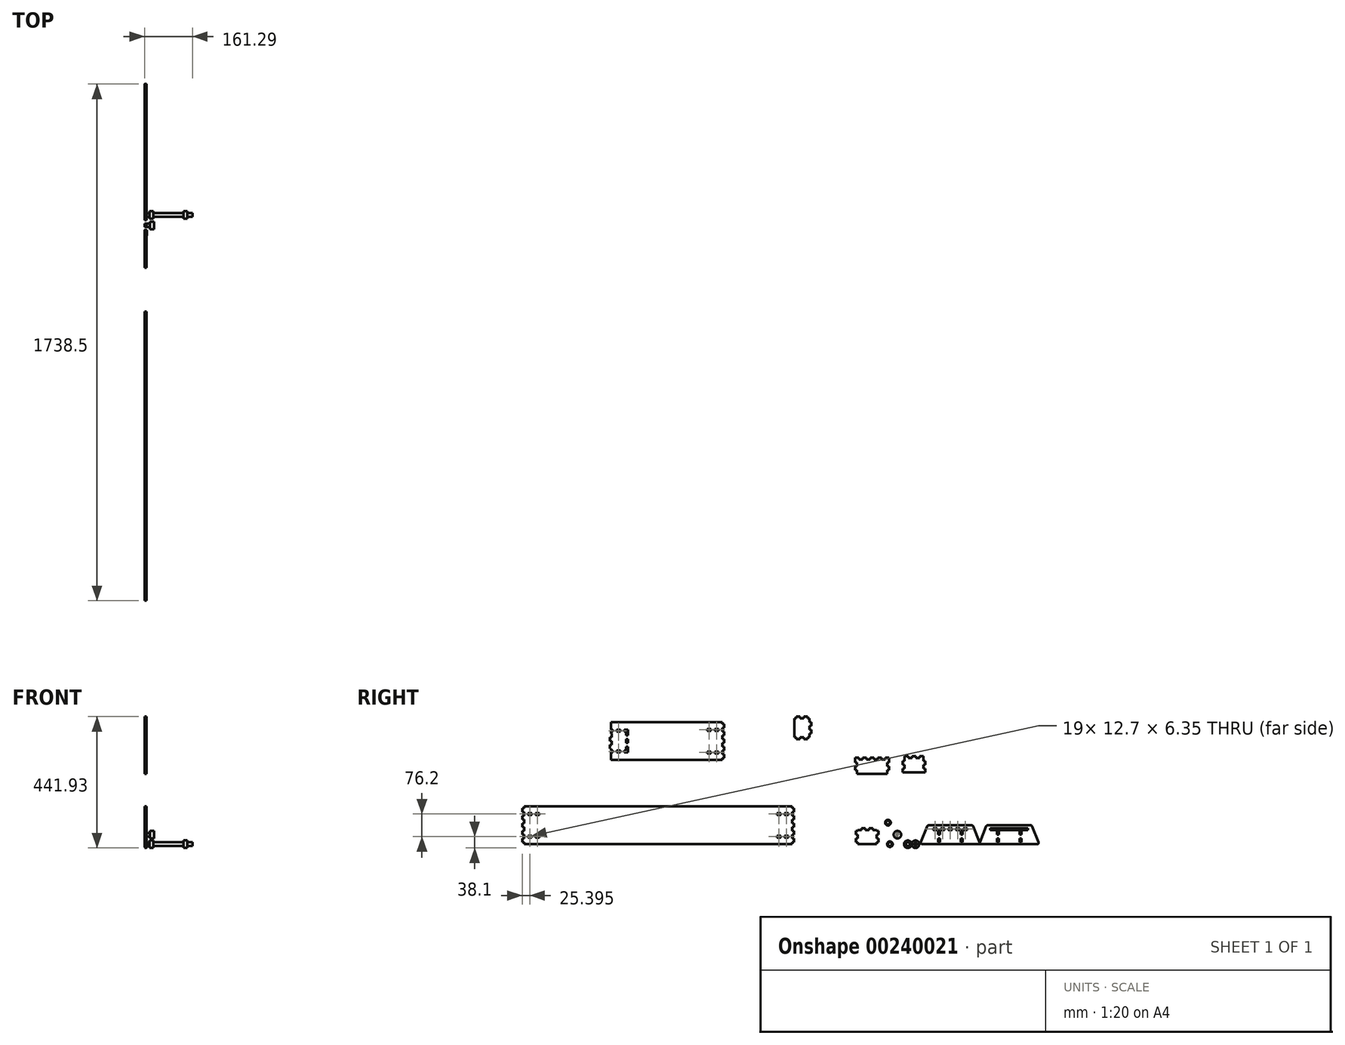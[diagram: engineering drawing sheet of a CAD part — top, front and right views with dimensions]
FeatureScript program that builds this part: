
annotation { "Feature Type Name" : "Feature", "Feature Type Description" : "" }
export const myFeature = defineFeature(function(context is Context, id is Id, definition is map)
    precondition{}
    {
        {
            var Q0;
            Q0=qCreatedBy(makeId("Right.planeOp"),FACE);
            var sketch = newSketch(context, id + "F0", { "sketchPlane" : qUnion([Q0])});
            skLineSegment(sketch, "E0.bottom", {"start": v(0, 0) * mm, "end": v(152.4, 0) * mm});
            skLineSegment(sketch, "E0.top", {"start": v(0, 101.6) * mm, "end": v(152.4, 101.6) * mm});
            skLineSegment(sketch, "E0.left", {"start": v(0, 0) * mm, "end": v(0, 101.6) * mm});
            skLineSegment(sketch, "E0.right", {"start": v(152.4, 0) * mm, "end": v(152.4, 101.6) * mm});
            skLineSegment(sketch, "E1", {"start": v(76.2, 101.6) * mm, "end": v(76.2, 0) * mm, "construction": true});
            skLineSegment(sketch, "E2", {"start": v(0, 50.8) * mm, "end": v(152.4, 50.8) * mm, "construction": true});
            skLineSegment(sketch, "E3", {"start": v(76.2, 53.98) * mm, "end": v(82.55, 53.98) * mm});
            skLineSegment(sketch, "E4", {"start": v(82.55, 53.98) * mm, "end": v(82.55, 50.8) * mm});
            skLineSegment(sketch, "E5.MirrorCS", {"start": v(69.85, 53.98) * mm, "end": v(69.85, 50.8) * mm});
            skLineSegment(sketch, "E6.MirrorCS", {"start": v(76.2, 53.98) * mm, "end": v(69.85, 53.98) * mm});
            skLineSegment(sketch, "E7.MirrorCS", {"start": v(82.55, 47.63) * mm, "end": v(82.55, 50.8) * mm});
            skLineSegment(sketch, "E8.MirrorCS", {"start": v(76.2, 47.63) * mm, "end": v(82.55, 47.63) * mm});
            skLineSegment(sketch, "E9.MirrorCS", {"start": v(76.2, 47.63) * mm, "end": v(69.85, 47.63) * mm});
            skLineSegment(sketch, "E10.MirrorCS", {"start": v(69.85, 47.63) * mm, "end": v(69.85, 50.8) * mm});
            skLineSegment(sketch, "E11.1.0.0", {"start": v(101.6, 53.98) * mm, "end": v(107.95, 53.98) * mm});
            skLineSegment(sketch, "E11.1.0.1", {"start": v(101.6, 53.98) * mm, "end": v(95.25, 53.98) * mm});
            skLineSegment(sketch, "E11.1.0.2", {"start": v(95.25, 53.98) * mm, "end": v(95.25, 50.8) * mm});
            skLineSegment(sketch, "E11.1.0.3", {"start": v(95.25, 47.63) * mm, "end": v(95.25, 50.8) * mm});
            skLineSegment(sketch, "E11.1.0.4", {"start": v(101.6, 47.63) * mm, "end": v(95.25, 47.63) * mm});
            skLineSegment(sketch, "E11.1.0.5", {"start": v(101.6, 47.63) * mm, "end": v(107.95, 47.63) * mm});
            skLineSegment(sketch, "E11.1.0.6", {"start": v(107.95, 47.63) * mm, "end": v(107.95, 50.8) * mm});
            skLineSegment(sketch, "E11.1.0.7", {"start": v(107.95, 53.98) * mm, "end": v(107.95, 50.8) * mm});
            skLineSegment(sketch, "E11.2.0.0", {"start": v(127, 53.98) * mm, "end": v(133.35, 53.98) * mm});
            skLineSegment(sketch, "E11.2.0.1", {"start": v(127, 53.98) * mm, "end": v(120.65, 53.98) * mm});
            skLineSegment(sketch, "E11.2.0.2", {"start": v(120.65, 53.98) * mm, "end": v(120.65, 50.8) * mm});
            skLineSegment(sketch, "E11.2.0.3", {"start": v(120.65, 47.63) * mm, "end": v(120.65, 50.8) * mm});
            skLineSegment(sketch, "E11.2.0.4", {"start": v(127, 47.63) * mm, "end": v(120.65, 47.63) * mm});
            skLineSegment(sketch, "E11.2.0.5", {"start": v(127, 47.63) * mm, "end": v(133.35, 47.63) * mm});
            skLineSegment(sketch, "E11.2.0.6", {"start": v(133.35, 47.63) * mm, "end": v(133.35, 50.8) * mm});
            skLineSegment(sketch, "E11.2.0.7", {"start": v(133.35, 53.98) * mm, "end": v(133.35, 50.8) * mm});
            skLineSegment(sketch, "E11.direction1", {"start": v(76.2, 53.98) * mm, "end": v(101.6, 53.98) * mm, "construction": true});
            skLineSegment(sketch, "E11.direction2", {"start": v(76.2, 53.98) * mm, "end": v(25.4, 53.98) * mm, "construction": true});
            skLineSegment(sketch, "E12.0.0.1", {"start": v(25.4, 53.97) * mm, "end": v(31.75, 53.98) * mm});
            skLineSegment(sketch, "E12.3.0.1", {"start": v(25.4, 53.97) * mm, "end": v(19.05, 53.97) * mm});
            skLineSegment(sketch, "E12.6.0.1", {"start": v(19.05, 53.98) * mm, "end": v(19.05, 50.8) * mm});
            skLineSegment(sketch, "E12.9.0.1", {"start": v(19.05, 47.62) * mm, "end": v(19.05, 50.8) * mm});
            skLineSegment(sketch, "E12.12.0.1", {"start": v(25.4, 47.63) * mm, "end": v(19.05, 47.63) * mm});
            skLineSegment(sketch, "E12.15.0.1", {"start": v(25.4, 47.63) * mm, "end": v(31.75, 47.63) * mm});
            skLineSegment(sketch, "E12.18.0.1", {"start": v(31.75, 47.62) * mm, "end": v(31.75, 50.8) * mm});
            skLineSegment(sketch, "E12.21.0.1", {"start": v(31.75, 53.98) * mm, "end": v(31.75, 50.8) * mm});
            skLineSegment(sketch, "E12.0.1.1", {"start": v(50.8, 53.97) * mm, "end": v(57.15, 53.98) * mm});
            skLineSegment(sketch, "E12.3.1.1", {"start": v(50.8, 53.97) * mm, "end": v(44.45, 53.97) * mm});
            skLineSegment(sketch, "E12.6.1.1", {"start": v(44.45, 53.98) * mm, "end": v(44.45, 50.8) * mm});
            skLineSegment(sketch, "E12.9.1.1", {"start": v(44.45, 47.62) * mm, "end": v(44.45, 50.8) * mm});
            skLineSegment(sketch, "E12.12.1.1", {"start": v(50.8, 47.63) * mm, "end": v(44.45, 47.63) * mm});
            skLineSegment(sketch, "E12.15.1.1", {"start": v(50.8, 47.63) * mm, "end": v(57.15, 47.63) * mm});
            skLineSegment(sketch, "E12.18.1.1", {"start": v(57.15, 47.62) * mm, "end": v(57.15, 50.8) * mm});
            skLineSegment(sketch, "E12.21.1.1", {"start": v(57.15, 53.98) * mm, "end": v(57.15, 50.8) * mm});
            skLineSegment(sketch, "E13.bottom", {"start": v(34.93, 44.45) * mm, "end": v(41.28, 44.45) * mm});
            skLineSegment(sketch, "E13.top", {"start": v(34.93, 31.75) * mm, "end": v(41.28, 31.75) * mm});
            skLineSegment(sketch, "E13.left", {"start": v(34.93, 44.45) * mm, "end": v(34.93, 31.75) * mm});
            skLineSegment(sketch, "E13.right", {"start": v(41.28, 44.45) * mm, "end": v(41.28, 31.75) * mm});
            skLineSegment(sketch, "E14.0.1.0", {"start": v(41.28, 19.05) * mm, "end": v(41.28, 6.35) * mm});
            skLineSegment(sketch, "E14.0.1.1", {"start": v(34.93, 19.05) * mm, "end": v(41.28, 19.05) * mm});
            skLineSegment(sketch, "E14.0.1.2", {"start": v(34.93, 19.05) * mm, "end": v(34.93, 6.35) * mm});
            skLineSegment(sketch, "E14.0.1.3", {"start": v(34.93, 6.35) * mm, "end": v(41.28, 6.35) * mm});
            skLineSegment(sketch, "E14.direction1", {"start": v(41.28, 31.75) * mm, "end": v(53.98, 31.75) * mm, "construction": true});
            skLineSegment(sketch, "E14.direction2", {"start": v(41.28, 31.75) * mm, "end": v(41.28, 6.35) * mm, "construction": true});
            skLineSegment(sketch, "E15.MirrorCS", {"start": v(111.12, 44.45) * mm, "end": v(111.12, 31.75) * mm});
            skLineSegment(sketch, "E16.MirrorCS", {"start": v(117.47, 44.45) * mm, "end": v(111.12, 44.45) * mm});
            skLineSegment(sketch, "E17.MirrorCS", {"start": v(117.47, 44.45) * mm, "end": v(117.47, 31.75) * mm});
            skLineSegment(sketch, "E18.MirrorCS", {"start": v(117.47, 31.75) * mm, "end": v(111.12, 31.75) * mm});
            skLineSegment(sketch, "E19.MirrorCS", {"start": v(117.47, 19.05) * mm, "end": v(111.12, 19.05) * mm});
            skLineSegment(sketch, "E20.MirrorCS", {"start": v(117.47, 19.05) * mm, "end": v(117.47, 6.35) * mm});
            skLineSegment(sketch, "E21.MirrorCS", {"start": v(117.47, 6.35) * mm, "end": v(111.12, 6.35) * mm});
            skLineSegment(sketch, "E22.MirrorCS", {"start": v(111.12, 31.75) * mm, "end": v(111.12, 6.35) * mm, "construction": true});
            skLineSegment(sketch, "E23", {"start": v(111.12, 19.05) * mm, "end": v(111.12, 6.35) * mm});
            skSolve(sketch);
        }
        {
            var Q0;
            Q0=makeQuery(id+"F0.imprint","IMPRINT",FACE,{"disambiguationData":[TD([[makeQuery(id+"F0.imprint","IMPRINT",EDGE,{"derivedFrom":sQuery(id+"F0.wireOp",EDGE,"E0.bottom")}),1.0]])]});
            extrude(context, id + "F1", {"entities" : qUnion([Q0]), "depth" : 6.35 * mm});
        }
        {
            var Q0;
            Q0=qCreatedBy(makeId("Right.planeOp"),FACE);
            var sketch = newSketch(context, id + "F2", { "sketchPlane" : qUnion([Q0])});
            skLineSegment(sketch, "E24.bottom", {"start": v(198.38, 0) * mm, "end": v(350.78, 0) * mm});
            skLineSegment(sketch, "E24.top", {"start": v(198.38, 101.6) * mm, "end": v(350.78, 101.6) * mm});
            skLineSegment(sketch, "E24.left", {"start": v(198.38, 0) * mm, "end": v(198.38, 101.6) * mm});
            skLineSegment(sketch, "E24.right", {"start": v(350.78, 0) * mm, "end": v(350.78, 101.6) * mm});
            skLineSegment(sketch, "E25", {"start": v(198.38, 50.8) * mm, "end": v(350.78, 50.8) * mm, "construction": true});
            skLineSegment(sketch, "E26.bottom", {"start": v(211.08, 53.98) * mm, "end": v(338.08, 53.98) * mm});
            skLineSegment(sketch, "E26.top", {"start": v(211.08, 47.63) * mm, "end": v(338.08, 47.63) * mm});
            skLineSegment(sketch, "E26.left", {"start": v(211.08, 53.98) * mm, "end": v(211.08, 47.63) * mm});
            skLineSegment(sketch, "E26.right", {"start": v(338.08, 53.98) * mm, "end": v(338.08, 47.63) * mm});
            skLineSegment(sketch, "E27.bottom", {"start": v(233.3, 44.45) * mm, "end": v(239.66, 44.45) * mm});
            skLineSegment(sketch, "E27.top", {"start": v(233.3, 31.75) * mm, "end": v(239.66, 31.75) * mm});
            skLineSegment(sketch, "E27.left", {"start": v(233.3, 44.45) * mm, "end": v(233.3, 31.75) * mm});
            skLineSegment(sketch, "E27.right", {"start": v(239.66, 44.45) * mm, "end": v(239.66, 31.75) * mm});
            skLineSegment(sketch, "E28.bottom", {"start": v(233.3, 19.05) * mm, "end": v(239.66, 19.05) * mm});
            skLineSegment(sketch, "E28.top", {"start": v(233.3, 6.35) * mm, "end": v(239.66, 6.35) * mm});
            skLineSegment(sketch, "E28.left", {"start": v(233.3, 19.05) * mm, "end": v(233.3, 6.35) * mm});
            skLineSegment(sketch, "E28.right", {"start": v(239.66, 19.05) * mm, "end": v(239.66, 6.35) * mm});
            skLineSegment(sketch, "E29", {"start": v(274.58, 101.6) * mm, "end": v(274.58, 0) * mm, "construction": true});
            skLineSegment(sketch, "E30.MirrorCS", {"start": v(315.86, 44.45) * mm, "end": v(309.5, 44.45) * mm});
            skLineSegment(sketch, "E31.MirrorCS", {"start": v(315.86, 31.75) * mm, "end": v(309.5, 31.75) * mm});
            skLineSegment(sketch, "E32.MirrorCS", {"start": v(315.86, 44.45) * mm, "end": v(315.86, 31.75) * mm});
            skLineSegment(sketch, "E33.MirrorCS", {"start": v(315.86, 19.05) * mm, "end": v(315.86, 6.35) * mm});
            skLineSegment(sketch, "E34.MirrorCS", {"start": v(315.86, 6.35) * mm, "end": v(309.5, 6.35) * mm});
            skLineSegment(sketch, "E35.MirrorCS", {"start": v(309.5, 19.05) * mm, "end": v(309.5, 6.35) * mm});
            skLineSegment(sketch, "E36.MirrorCS", {"start": v(309.5, 44.45) * mm, "end": v(309.5, 31.75) * mm});
            skLineSegment(sketch, "E37.MirrorCS", {"start": v(315.86, 19.05) * mm, "end": v(309.5, 19.05) * mm});
            skSolve(sketch);
        }
        {
            var Q0;
            Q0=makeQuery(id+"F2.imprint","IMPRINT",FACE,{"disambiguationData":[TD([[makeQuery(id+"F2.imprint","IMPRINT",EDGE,{"derivedFrom":sQuery(id+"F2.wireOp",EDGE,"E24.bottom")}),1.0]])]});
            extrude(context, id + "F3", {"entities" : qUnion([Q0]), "depth" : 6.35 * mm});
        }
        {
            var Q0;
            Q0=qCreatedBy(makeId("Right.planeOp"),FACE);
            var sketch = newSketch(context, id + "F4", { "sketchPlane" : qUnion([Q0])});
            skLineSegment(sketch, "E38.bottom", {"start": v(-164.83, 0) * mm, "end": v(-241.03, 0) * mm});
            skLineSegment(sketch, "E38.top", {"start": v(-164.83, 53.98) * mm, "end": v(-241.03, 53.98) * mm});
            skLineSegment(sketch, "E38.left", {"start": v(-164.83, 0) * mm, "end": v(-164.83, 53.97) * mm});
            skLineSegment(sketch, "E38.right", {"start": v(-241.03, 0) * mm, "end": v(-241.03, 53.98) * mm});
            skLineSegment(sketch, "E39.bottom", {"start": v(-164.83, 0) * mm, "end": v(-171.18, 0) * mm});
            skLineSegment(sketch, "E39.top", {"start": v(-164.83, 6.35) * mm, "end": v(-171.18, 6.35) * mm});
            skLineSegment(sketch, "E39.left", {"start": v(-164.83, 0) * mm, "end": v(-164.83, 6.35) * mm});
            skLineSegment(sketch, "E39.right", {"start": v(-171.18, 0) * mm, "end": v(-171.18, 6.35) * mm});
            skLineSegment(sketch, "E40.bottom", {"start": v(-164.83, 19.05) * mm, "end": v(-171.18, 19.05) * mm});
            skLineSegment(sketch, "E40.top", {"start": v(-164.83, 31.75) * mm, "end": v(-171.18, 31.75) * mm});
            skLineSegment(sketch, "E40.left", {"start": v(-164.83, 19.05) * mm, "end": v(-164.83, 31.75) * mm});
            skLineSegment(sketch, "E40.right", {"start": v(-171.18, 19.05) * mm, "end": v(-171.18, 31.75) * mm});
            skLineSegment(sketch, "E41.bottom", {"start": v(-164.83, 53.98) * mm, "end": v(-171.18, 53.98) * mm});
            skLineSegment(sketch, "E41.top", {"start": v(-164.83, 47.62) * mm, "end": v(-171.18, 47.62) * mm});
            skLineSegment(sketch, "E41.left", {"start": v(-164.83, 53.98) * mm, "end": v(-164.83, 47.62) * mm});
            skLineSegment(sketch, "E42", {"start": v(-202.93, 53.98) * mm, "end": v(-202.93, 0) * mm, "construction": true});
            skLineSegment(sketch, "E43.MirrorCS", {"start": v(-241.03, 47.62) * mm, "end": v(-234.68, 47.62) * mm});
            skLineSegment(sketch, "E44.MirrorCS", {"start": v(-234.68, 53.98) * mm, "end": v(-234.68, 47.62) * mm});
            skLineSegment(sketch, "E45.MirrorCS", {"start": v(-234.68, 19.05) * mm, "end": v(-234.68, 31.75) * mm});
            skLineSegment(sketch, "E46.MirrorCS", {"start": v(-241.03, 31.75) * mm, "end": v(-234.68, 31.75) * mm});
            skLineSegment(sketch, "E47.MirrorCS", {"start": v(-241.03, 19.05) * mm, "end": v(-234.68, 19.05) * mm});
            skLineSegment(sketch, "E48.MirrorCS", {"start": v(-234.68, 0) * mm, "end": v(-234.68, 6.35) * mm});
            skLineSegment(sketch, "E49.MirrorCS", {"start": v(-241.03, 6.35) * mm, "end": v(-234.68, 6.35) * mm});
            skLineSegment(sketch, "E50.bottom", {"start": v(-183.88, 53.98) * mm, "end": v(-196.58, 53.98) * mm});
            skLineSegment(sketch, "E51.bottom", {"start": v(-171.18, 53.98) * mm, "end": v(-183.88, 53.98) * mm});
            skLineSegment(sketch, "E51.top", {"start": v(-171.18, 47.62) * mm, "end": v(-183.88, 47.62) * mm});
            skLineSegment(sketch, "E51.left", {"start": v(-171.18, 53.98) * mm, "end": v(-171.18, 47.62) * mm});
            skLineSegment(sketch, "E51.right", {"start": v(-183.88, 53.98) * mm, "end": v(-183.88, 47.62) * mm});
            skLineSegment(sketch, "E52.MirrorCS", {"start": v(-234.68, 47.62) * mm, "end": v(-221.98, 47.62) * mm});
            skLineSegment(sketch, "E53.MirrorCS", {"start": v(-221.98, 53.98) * mm, "end": v(-221.98, 47.62) * mm});
            skLineSegment(sketch, "E54.bottom", {"start": v(-196.58, 53.98) * mm, "end": v(-202.93, 53.98) * mm});
            skLineSegment(sketch, "E54.top", {"start": v(-196.58, 47.62) * mm, "end": v(-202.93, 47.62) * mm});
            skLineSegment(sketch, "E54.left", {"start": v(-196.58, 53.98) * mm, "end": v(-196.58, 47.62) * mm});
            skLineSegment(sketch, "E54.right", {"start": v(-202.93, 53.98) * mm, "end": v(-202.93, 47.62) * mm});
            skLineSegment(sketch, "E55.MirrorCS", {"start": v(-209.28, 47.62) * mm, "end": v(-202.93, 47.62) * mm});
            skLineSegment(sketch, "E56.MirrorCS", {"start": v(-209.28, 53.98) * mm, "end": v(-209.28, 47.62) * mm});
            skLineSegment(sketch, "E57.top", {"start": v(-164.83, 44.45) * mm, "end": v(-171.18, 44.45) * mm});
            skLineSegment(sketch, "E57.left", {"start": v(-164.83, 47.62) * mm, "end": v(-164.83, 44.45) * mm});
            skLineSegment(sketch, "E57.right", {"start": v(-171.18, 47.62) * mm, "end": v(-171.18, 44.45) * mm});
            skLineSegment(sketch, "E58.MirrorCS", {"start": v(-234.68, 47.62) * mm, "end": v(-234.68, 44.45) * mm});
            skLineSegment(sketch, "E59.MirrorCS", {"start": v(-241.03, 44.45) * mm, "end": v(-234.68, 44.45) * mm});
            skSolve(sketch);
        }
        {
            var Q0;
            {var subQ4=sQuery(id+"F4.wireOp",EDGE,"E39.top");Q0=makeQuery(id+"F4.imprint","IMPRINT",FACE,{"disambiguationData":[TD([[makeQuery(id+"F4.imprint","IMPRINT",EDGE,{"derivedFrom":subQ4}),-1.0]])]});}
            extrude(context, id + "F5", {"entities" : qUnion([Q0]), "depth" : 6.35 * mm});
        }
        {
            var Q0;
            Q0=qCreatedBy(makeId("Right.planeOp"),FACE);
            var sketch = newSketch(context, id + "F6", { "sketchPlane" : qUnion([Q0])});
            skLineSegment(sketch, "E60.bottom", {"start": v(-450.34, 0) * mm, "end": v(-1364.74, 0) * mm});
            skLineSegment(sketch, "E60.top", {"start": v(-450.34, 127) * mm, "end": v(-1364.74, 127) * mm});
            skLineSegment(sketch, "E60.left", {"start": v(-450.34, 0) * mm, "end": v(-450.34, 127) * mm});
            skLineSegment(sketch, "E60.right", {"start": v(-1364.74, 0) * mm, "end": v(-1364.74, 127) * mm});
            skLineSegment(sketch, "E61.bottom", {"start": v(-450.34, 127) * mm, "end": v(-456.7, 127) * mm});
            skLineSegment(sketch, "E61.top", {"start": v(-450.34, 120.65) * mm, "end": v(-456.7, 120.65) * mm});
            skLineSegment(sketch, "E61.left", {"start": v(-450.34, 127) * mm, "end": v(-450.34, 120.65) * mm});
            skLineSegment(sketch, "E61.right", {"start": v(-456.7, 127) * mm, "end": v(-456.7, 120.65) * mm});
            skLineSegment(sketch, "E62.bottom", {"start": v(-450.34, 107.95) * mm, "end": v(-456.7, 107.95) * mm});
            skLineSegment(sketch, "E62.top", {"start": v(-450.34, 95.25) * mm, "end": v(-456.7, 95.25) * mm});
            skLineSegment(sketch, "E62.left", {"start": v(-450.34, 107.95) * mm, "end": v(-450.34, 95.25) * mm});
            skLineSegment(sketch, "E62.right", {"start": v(-456.7, 107.95) * mm, "end": v(-456.7, 95.25) * mm});
            skLineSegment(sketch, "E63.0.1.0", {"start": v(-456.7, 82.55) * mm, "end": v(-456.7, 69.85) * mm});
            skLineSegment(sketch, "E63.0.1.1", {"start": v(-450.34, 69.85) * mm, "end": v(-456.7, 69.85) * mm});
            skLineSegment(sketch, "E63.0.1.2", {"start": v(-450.34, 82.55) * mm, "end": v(-456.7, 82.55) * mm});
            skLineSegment(sketch, "E63.0.2.0", {"start": v(-456.7, 57.15) * mm, "end": v(-456.7, 44.45) * mm});
            skLineSegment(sketch, "E63.0.2.1", {"start": v(-450.34, 44.45) * mm, "end": v(-456.7, 44.45) * mm});
            skLineSegment(sketch, "E63.0.2.2", {"start": v(-450.34, 57.15) * mm, "end": v(-456.7, 57.15) * mm});
            skLineSegment(sketch, "E63.0.3.0", {"start": v(-456.7, 31.75) * mm, "end": v(-456.7, 19.05) * mm});
            skLineSegment(sketch, "E63.0.3.1", {"start": v(-450.34, 19.05) * mm, "end": v(-456.7, 19.05) * mm});
            skLineSegment(sketch, "E63.0.3.2", {"start": v(-450.34, 31.75) * mm, "end": v(-456.7, 31.75) * mm});
            skLineSegment(sketch, "E63.direction1", {"start": v(-456.7, 95.25) * mm, "end": v(-431.3, 95.25) * mm, "construction": true});
            skLineSegment(sketch, "E63.direction2", {"start": v(-456.7, 95.25) * mm, "end": v(-456.7, 69.85) * mm, "construction": true});
            skLineSegment(sketch, "E64", {"start": v(-450.34, 63.5) * mm, "end": v(-1364.74, 63.5) * mm, "construction": true});
            skLineSegment(sketch, "E65.MirrorCS", {"start": v(-450.34, 6.35) * mm, "end": v(-456.7, 6.35) * mm});
            skLineSegment(sketch, "E66.MirrorCS", {"start": v(-456.7, 0) * mm, "end": v(-456.7, 6.35) * mm});
            skLineSegment(sketch, "E67.left", {"start": v(-456.7, 104.78) * mm, "end": v(-456.7, 98.43) * mm});
            skLineSegment(sketch, "E68.direction1", {"start": v(-456.7, 69.85) * mm, "end": v(-482.1, 69.85) * mm, "construction": true});
            skLineSegment(sketch, "E69.MirrorCS", {"start": v(-456.7, 31.75) * mm, "end": v(-456.7, 57.15) * mm, "construction": true});
            skLineSegment(sketch, "E70", {"start": v(-907.54, 0) * mm, "end": v(-907.54, 127) * mm, "construction": true});
            skLineSegment(sketch, "E71.MirrorCS", {"start": v(-1364.74, 127) * mm, "end": v(-1358.4, 127) * mm});
            skLineSegment(sketch, "E72.MirrorCS", {"start": v(-1358.4, 104.77) * mm, "end": v(-1358.4, 98.42) * mm});
            skLineSegment(sketch, "E73.MirrorCS", {"start": v(-1358.4, 82.55) * mm, "end": v(-1358.4, 69.85) * mm});
            skLineSegment(sketch, "E74.MirrorCS", {"start": v(-1364.74, 95.25) * mm, "end": v(-1358.4, 95.25) * mm});
            skLineSegment(sketch, "E75.MirrorCS", {"start": v(-1364.74, 107.95) * mm, "end": v(-1358.4, 107.95) * mm});
            skLineSegment(sketch, "E76.MirrorCS", {"start": v(-1364.74, 120.65) * mm, "end": v(-1358.4, 120.65) * mm});
            skLineSegment(sketch, "E77.MirrorCS", {"start": v(-1358.4, 127) * mm, "end": v(-1358.4, 120.65) * mm});
            skLineSegment(sketch, "E78.MirrorCS", {"start": v(-1364.74, 127) * mm, "end": v(-1364.74, 120.65) * mm});
            skLineSegment(sketch, "E79.MirrorCS", {"start": v(-1364.74, 19.05) * mm, "end": v(-1358.4, 19.05) * mm});
            skLineSegment(sketch, "E80.MirrorCS", {"start": v(-1364.74, 44.45) * mm, "end": v(-1358.4, 44.45) * mm});
            skLineSegment(sketch, "E81.MirrorCS", {"start": v(-1358.4, 107.95) * mm, "end": v(-1358.4, 95.25) * mm});
            skLineSegment(sketch, "E82.MirrorCS", {"start": v(-1364.74, 31.75) * mm, "end": v(-1358.4, 31.75) * mm});
            skLineSegment(sketch, "E83.MirrorCS", {"start": v(-1364.74, 57.15) * mm, "end": v(-1358.4, 57.15) * mm});
            skLineSegment(sketch, "E84.MirrorCS", {"start": v(-1364.74, 6.35) * mm, "end": v(-1358.4, 6.35) * mm});
            skLineSegment(sketch, "E85.MirrorCS", {"start": v(-1364.74, 82.55) * mm, "end": v(-1358.4, 82.55) * mm});
            skLineSegment(sketch, "E86.MirrorCS", {"start": v(-1364.74, 69.85) * mm, "end": v(-1358.4, 69.85) * mm});
            skLineSegment(sketch, "E87.MirrorCS", {"start": v(-1358.4, 95.25) * mm, "end": v(-1358.4, 69.85) * mm, "construction": true});
            skLineSegment(sketch, "E88.MirrorCS", {"start": v(-1358.4, 0) * mm, "end": v(-1358.4, 6.35) * mm});
            skLineSegment(sketch, "E89.MirrorCS", {"start": v(-1358.4, 57.15) * mm, "end": v(-1358.4, 44.45) * mm});
            skLineSegment(sketch, "E90.MirrorCS", {"start": v(-1358.4, 69.85) * mm, "end": v(-1333, 69.85) * mm, "construction": true});
            skLineSegment(sketch, "E91.MirrorCS", {"start": v(-1364.74, 107.95) * mm, "end": v(-1364.74, 95.25) * mm});
            skLineSegment(sketch, "E92.MirrorCS", {"start": v(-1358.4, 31.75) * mm, "end": v(-1358.4, 19.05) * mm});
            skLineSegment(sketch, "E93.MirrorCS", {"start": v(-1364.74, 63.5) * mm, "end": v(-450.34, 63.5) * mm, "construction": true});
            skLineSegment(sketch, "E94.MirrorCS", {"start": v(-1358.4, 31.75) * mm, "end": v(-1358.4, 57.15) * mm, "construction": true});
            skLineSegment(sketch, "E95.MirrorCS", {"start": v(-1358.4, 95.25) * mm, "end": v(-1383.8, 95.25) * mm, "construction": true});
            skLineSegment(sketch, "E96.MirrorCS", {"start": v(-1364.74, 127) * mm, "end": v(-450.34, 127) * mm});
            skLineSegment(sketch, "E97.MirrorCS", {"start": v(-1364.74, 0) * mm, "end": v(-450.34, 0) * mm});
            skLineSegment(sketch, "E98", {"start": v(-456.7, 28.58) * mm, "end": v(-456.7, 22.23) * mm});
            skLineSegment(sketch, "E99", {"start": v(-1358.4, 28.57) * mm, "end": v(-1358.4, 22.22) * mm});
            skLineSegment(sketch, "E100.bottom", {"start": v(-469.4, 104.78) * mm, "end": v(-482.1, 104.78) * mm});
            skLineSegment(sketch, "E100.top", {"start": v(-469.4, 98.43) * mm, "end": v(-482.1, 98.43) * mm});
            skLineSegment(sketch, "E100.left", {"start": v(-469.4, 104.78) * mm, "end": v(-469.4, 98.43) * mm});
            skLineSegment(sketch, "E100.right", {"start": v(-482.1, 104.78) * mm, "end": v(-482.1, 98.43) * mm});
            skLineSegment(sketch, "E101.1.0.0", {"start": v(-494.8, 104.78) * mm, "end": v(-494.8, 98.43) * mm});
            skLineSegment(sketch, "E101.1.0.1", {"start": v(-507.5, 104.78) * mm, "end": v(-507.5, 98.43) * mm});
            skLineSegment(sketch, "E101.1.0.2", {"start": v(-494.8, 98.43) * mm, "end": v(-507.5, 98.43) * mm});
            skLineSegment(sketch, "E101.1.0.3", {"start": v(-494.8, 104.78) * mm, "end": v(-507.5, 104.78) * mm});
            skLineSegment(sketch, "E101.direction1", {"start": v(-482.1, 98.43) * mm, "end": v(-507.5, 98.43) * mm, "construction": true});
            skLineSegment(sketch, "E102.MirrorCS", {"start": v(-494.8, 28.57) * mm, "end": v(-507.5, 28.57) * mm});
            skLineSegment(sketch, "E103.MirrorCS", {"start": v(-507.5, 22.23) * mm, "end": v(-507.5, 28.58) * mm});
            skLineSegment(sketch, "E104.MirrorCS", {"start": v(-482.1, 28.57) * mm, "end": v(-507.5, 28.57) * mm, "construction": true});
            skLineSegment(sketch, "E105.MirrorCS", {"start": v(-482.1, 22.23) * mm, "end": v(-482.1, 28.58) * mm});
            skLineSegment(sketch, "E106.MirrorCS", {"start": v(-469.4, 22.23) * mm, "end": v(-469.4, 28.58) * mm});
            skLineSegment(sketch, "E107.MirrorCS", {"start": v(-469.4, 28.57) * mm, "end": v(-482.1, 28.57) * mm});
            skLineSegment(sketch, "E108.MirrorCS", {"start": v(-469.4, 22.22) * mm, "end": v(-482.1, 22.22) * mm});
            skLineSegment(sketch, "E109.MirrorCS", {"start": v(-494.8, 22.23) * mm, "end": v(-494.8, 28.58) * mm});
            skLineSegment(sketch, "E110.MirrorCS", {"start": v(-494.8, 22.22) * mm, "end": v(-507.5, 22.22) * mm});
            skLineSegment(sketch, "E111.MirrorCS", {"start": v(-1307.6, 104.77) * mm, "end": v(-1307.6, 98.42) * mm});
            skLineSegment(sketch, "E112.MirrorCS", {"start": v(-1320.3, 22.22) * mm, "end": v(-1320.3, 28.57) * mm});
            skLineSegment(sketch, "E113.MirrorCS", {"start": v(-1333, 22.22) * mm, "end": v(-1333, 28.57) * mm});
            skLineSegment(sketch, "E114.MirrorCS", {"start": v(-1307.6, 22.22) * mm, "end": v(-1307.6, 28.57) * mm});
            skLineSegment(sketch, "E115.MirrorCS", {"start": v(-1345.7, 104.77) * mm, "end": v(-1345.7, 98.42) * mm});
            skLineSegment(sketch, "E116.MirrorCS", {"start": v(-1333, 104.77) * mm, "end": v(-1333, 98.42) * mm});
            skLineSegment(sketch, "E117.MirrorCS", {"start": v(-1345.7, 22.22) * mm, "end": v(-1345.7, 28.57) * mm});
            skLineSegment(sketch, "E118.MirrorCS", {"start": v(-1320.3, 104.77) * mm, "end": v(-1320.3, 98.42) * mm});
            skLineSegment(sketch, "E119.MirrorCS", {"start": v(-1320.3, 28.57) * mm, "end": v(-1307.6, 28.57) * mm});
            skLineSegment(sketch, "E120.MirrorCS", {"start": v(-1345.7, 98.43) * mm, "end": v(-1333, 98.43) * mm});
            skLineSegment(sketch, "E121.MirrorCS", {"start": v(-1345.7, 104.78) * mm, "end": v(-1333, 104.78) * mm});
            skLineSegment(sketch, "E122.MirrorCS", {"start": v(-1320.3, 104.78) * mm, "end": v(-1307.6, 104.78) * mm});
            skLineSegment(sketch, "E123.MirrorCS", {"start": v(-1320.3, 98.43) * mm, "end": v(-1307.6, 98.43) * mm});
            skLineSegment(sketch, "E124.MirrorCS", {"start": v(-1333, 28.57) * mm, "end": v(-1307.6, 28.57) * mm, "construction": true});
            skLineSegment(sketch, "E125.MirrorCS", {"start": v(-1345.7, 28.57) * mm, "end": v(-1333, 28.57) * mm});
            skLineSegment(sketch, "E126.MirrorCS", {"start": v(-1320.3, 22.22) * mm, "end": v(-1307.6, 22.22) * mm});
            skLineSegment(sketch, "E127.MirrorCS", {"start": v(-1345.7, 22.22) * mm, "end": v(-1333, 22.22) * mm});
            skLineSegment(sketch, "E128.MirrorCS", {"start": v(-1333, 98.43) * mm, "end": v(-1307.6, 98.43) * mm, "construction": true});
            skSolve(sketch);
        }
        {
            var Q0;
            {var subQ4=sQuery(id+"F6.wireOp",EDGE,"E61.top");Q0=makeQuery(id+"F6.imprint","IMPRINT",FACE,{"disambiguationData":[TD([[makeQuery(id+"F6.imprint","IMPRINT",EDGE,{"derivedFrom":subQ4}),1.0]])]});}
            extrude(context, id + "F7", {"entities" : qUnion([Q0]), "depth" : 6.35 * mm});
        }
        {
            var Q0;
            Q0=qCreatedBy(makeId("Right.planeOp"),FACE);
            var sketch = newSketch(context, id + "F8", { "sketchPlane" : qUnion([Q0])});
            skCircle(sketch, "E129", {"center": v(-101.6, 32.09) * mm, "radius": 5.72 * mm});
            skSolve(sketch);
        }
        {
            var Q0;
            Q0=makeQuery(id+"F8.imprint","IMPRINT",FACE,{"disambiguationData":[TD([[makeQuery(id+"F8.imprint","IMPRINT",EDGE,{"derivedFrom":sQuery(id+"F8.wireOp",EDGE,"E129")}),1.0]])]});
            extrude(context, id + "F9", {"entities" : qUnion([Q0]), "depth" : 19.05 * mm});
        }
        {
            var Q0;
            Q0=qCreatedBy(makeId("Right.planeOp"),FACE);
            var sketch = newSketch(context, id + "F10", { "sketchPlane" : qUnion([Q0])});
            skCircle(sketch, "E130", {"center": v(-66.73, 0) * mm, "radius": 5.72 * mm});
            skSolve(sketch);
        }
        {
            var Q0;
            Q0=makeQuery(id+"F10.imprint","IMPRINT",FACE,{"disambiguationData":[TD([[makeQuery(id+"F10.imprint","IMPRINT",EDGE,{"derivedFrom":sQuery(id+"F10.wireOp",EDGE,"E130")}),1.0]])]});
            extrude(context, id + "F11", {"entities" : qUnion([Q0]), "depth" : 17.14 * mm});
        }
        {
            var Q0;
            Q0=makeQuery(id+"F11.opExtrude","CAP_FACE",FACE,{"disambiguationData":[OSD([sQuery(id+"F10.wireOp",EDGE,"E130")])],"isStart":false});
            var sketch = newSketch(context, id + "F12", { "sketchPlane" : qUnion([Q0])});
            skCircle(sketch, "E131", {"center": v(-66.73, 0) * mm, "radius": 12.7 * mm});
            skSolve(sketch);
        }
        {
            var Q0;
            Q0=makeQuery(id+"F12.imprint","IMPRINT",FACE,{"disambiguationData":[TD([[makeQuery(id+"F12.imprint","IMPRINT",EDGE,{"derivedFrom":sQuery(id+"F12.wireOp",EDGE,"E131")}),1.0]])]});
            var Q1;
            Q1=makeQuery(id+"F12.imprint","IMPRINT",FACE,{"disambiguationData":[TD([[makeQuery(id+"F12.imprint","IMPRINT",EDGE,{"derivedFrom":makeQuery(id+"F11.opExtrude","CAP_EDGE",EDGE,{"disambiguationData":[OSD([sQuery(id+"F10.wireOp",EDGE,"E130")])],"isStart":false})}),1.0]])]});
            extrude(context, id + "F13", {"entities" : qUnion([Q0, Q1]), "operationType" : NewBodyOperationType.ADD, "depth" : 12.7 * mm});
        }
        {
            var Q0;
            Q0=makeQuery(id+"F13.opExtrude","CAP_FACE",FACE,{"disambiguationData":[OSD([sQuery(id+"F12.wireOp",EDGE,"E131")])],"isStart":false});
            var sketch = newSketch(context, id + "F14", { "sketchPlane" : qUnion([Q0])});
            skCircle(sketch, "E132", {"center": v(-66.73, 0) * mm, "radius": 6.35 * mm});
            skSolve(sketch);
        }
        {
            var Q0;
            Q0=makeQuery(id+"F14.imprint","IMPRINT",FACE,{"disambiguationData":[TD([[makeQuery(id+"F14.imprint","IMPRINT",EDGE,{"derivedFrom":sQuery(id+"F14.wireOp",EDGE,"E132")}),1.0]])]});
            extrude(context, id + "F15", {"entities" : qUnion([Q0]), "operationType" : NewBodyOperationType.ADD, "depth" : 101.6 * mm});
        }
        {
            var Q0;
            Q0=makeQuery(id+"F15.opExtrude","CAP_FACE",FACE,{"disambiguationData":[OSD([sQuery(id+"F14.wireOp",EDGE,"E132")])],"isStart":false});
            var sketch = newSketch(context, id + "F16", { "sketchPlane" : qUnion([Q0])});
            skCircle(sketch, "E133", {"center": v(-66.73, 0) * mm, "radius": 12.7 * mm});
            skSolve(sketch);
        }
        {
            var Q0;
            Q0=makeQuery(id+"F16.imprint","IMPRINT",FACE,{"disambiguationData":[TD([[makeQuery(id+"F16.imprint","IMPRINT",EDGE,{"derivedFrom":sQuery(id+"F16.wireOp",EDGE,"E133")}),1.0]])]});
            var Q1;
            Q1=makeQuery(id+"F16.imprint","IMPRINT",FACE,{"disambiguationData":[TD([[makeQuery(id+"F16.imprint","IMPRINT",EDGE,{"derivedFrom":makeQuery(id+"F15.opExtrude","CAP_EDGE",EDGE,{"disambiguationData":[OSD([sQuery(id+"F14.wireOp",EDGE,"E132")])],"isStart":false})}),1.0]])]});
            extrude(context, id + "F17", {"entities" : qUnion([Q0, Q1]), "operationType" : NewBodyOperationType.ADD, "depth" : 12.7 * mm});
        }
        {
            var Q0;
            Q0=makeQuery(id+"F17.opExtrude","CAP_FACE",FACE,{"disambiguationData":[OSD([sQuery(id+"F16.wireOp",EDGE,"E133")])],"isStart":false});
            var sketch = newSketch(context, id + "F18", { "sketchPlane" : qUnion([Q0])});
            skCircle(sketch, "E134", {"center": v(-66.73, 0) * mm, "radius": 6.35 * mm});
            skSolve(sketch);
        }
        {
            var Q0;
            Q0=makeQuery(id+"F18.imprint","IMPRINT",FACE,{"disambiguationData":[TD([[makeQuery(id+"F18.imprint","IMPRINT",EDGE,{"derivedFrom":sQuery(id+"F18.wireOp",EDGE,"E134")}),1.0]])]});
            extrude(context, id + "F19", {"entities" : qUnion([Q0]), "operationType" : NewBodyOperationType.ADD, "depth" : 17.14 * mm});
        }
        {
            var Q0;
            Q0=makeQuery(id+"F9.opExtrude","CAP_FACE",FACE,{"disambiguationData":[OSD([sQuery(id+"F8.wireOp",EDGE,"E129")])],"isStart":false});
            var sketch = newSketch(context, id + "F20", { "sketchPlane" : qUnion([Q0])});
            skCircle(sketch, "E135", {"center": v(-101.6, 32.09) * mm, "radius": 12.7 * mm});
            skSolve(sketch);
        }
        {
            var Q0;
            Q0=makeQuery(id+"F20.imprint","IMPRINT",FACE,{"disambiguationData":[TD([[makeQuery(id+"F20.imprint","IMPRINT",EDGE,{"derivedFrom":sQuery(id+"F20.wireOp",EDGE,"E135")}),1.0]])]});
            var Q1;
            Q1=makeQuery(id+"F20.imprint","IMPRINT",FACE,{"disambiguationData":[TD([[makeQuery(id+"F20.imprint","IMPRINT",EDGE,{"derivedFrom":makeQuery(id+"F9.opExtrude","CAP_EDGE",EDGE,{"disambiguationData":[OSD([sQuery(id+"F8.wireOp",EDGE,"E129")])],"isStart":false})}),1.0]])]});
            extrude(context, id + "F21", {"entities" : qUnion([Q0, Q1]), "operationType" : NewBodyOperationType.ADD, "depth" : 12.7 * mm});
        }
        {
            var Q0;
            Q0=qCreatedBy(makeId("Top.planeOp"),FACE);
            var sketch = newSketch(context, id + "F22", { "sketchPlane" : qUnion([Q0])});
            skCircle(sketch, "E136", {"center": v(4.76, -101.6) * mm, "radius": 1.59 * mm});
            skSolve(sketch);
        }
        {
            var Q0;
            Q0 = qSketchRegion(id + "F22", true);
            extrude(context, id + "F23", {"entities" : qUnion([Q0]), "operationType" : NewBodyOperationType.REMOVE, "endBound" : BoundingType.THROUGH_ALL, "depth" : 25.4 * mm});
        }
        {
            var Q0;
            Q0=qCreatedBy(makeId("Right.planeOp"),FACE);
            var sketch = newSketch(context, id + "F24", { "sketchPlane" : qUnion([Q0])});
            skCircle(sketch, "E137", {"center": v(-127, 0) * mm, "radius": 9.53 * mm});
            skSolve(sketch);
        }
        {
            var Q0;
            Q0=makeQuery(id+"F24.imprint","IMPRINT",FACE,{"disambiguationData":[TD([[makeQuery(id+"F24.imprint","IMPRINT",EDGE,{"derivedFrom":sQuery(id+"F24.wireOp",EDGE,"E137")}),1.0]])]});
            extrude(context, id + "F25", {"entities" : qUnion([Q0]), "depth" : 8.47 * mm});
        }
        {
            var Q0;
            Q0=qCreatedBy(makeId("Top.planeOp"),FACE);
            var sketch = newSketch(context, id + "F26", { "sketchPlane" : qUnion([Q0])});
            skCircle(sketch, "E138", {"center": v(4.23, -127) * mm, "radius": 1.59 * mm});
            skSolve(sketch);
        }
        {
            var Q0;
            Q0 = qSketchRegion(id + "F26", true);
            extrude(context, id + "F27", {"entities" : qUnion([Q0]), "operationType" : NewBodyOperationType.REMOVE, "endBound" : BoundingType.THROUGH_ALL, "depth" : 25.4 * mm});
        }
        {
            var Q0;
            Q0=makeQuery(id+"F25.opExtrude","CAP_FACE",FACE,{"disambiguationData":[OSD([sQuery(id+"F24.wireOp",EDGE,"E137")])],"isStart":true});
            var sketch = newSketch(context, id + "F28", { "sketchPlane" : qUnion([Q0])});
            skCircle(sketch, "E139", {"center": v(127, 0) * mm, "radius": 6.35 * mm});
            skSolve(sketch);
        }
        {
            var Q0;
            Q0=makeQuery(id+"F28.imprint","IMPRINT",FACE,{"disambiguationData":[TD([[makeQuery(id+"F28.imprint","IMPRINT",EDGE,{"derivedFrom":sQuery(id+"F28.wireOp",EDGE,"E139")}),1.0]])]});
            extrude(context, id + "F29", {"entities" : qUnion([Q0]), "operationType" : NewBodyOperationType.REMOVE, "endBound" : BoundingType.UP_TO_NEXT, "oppositeDirection" : true, "depth" : 25.4 * mm});
        }
        {
            var Q0;
            Q0=qCreatedBy(makeId("Right.planeOp"),FACE);
            var sketch = newSketch(context, id + "F30", { "sketchPlane" : qUnion([Q0])});
            skCircle(sketch, "E140", {"center": v(-133.45, 72.65) * mm, "radius": 9.53 * mm});
            skCircle(sketch, "E141", {"center": v(-133.45, 72.65) * mm, "radius": 6.35 * mm});
            skSolve(sketch);
        }
        {
            var Q0;
            Q0=makeQuery(id+"F30.imprint","IMPRINT",FACE,{"disambiguationData":[TD([[makeQuery(id+"F30.imprint","IMPRINT",EDGE,{"derivedFrom":sQuery(id+"F30.wireOp",EDGE,"E140")}),1.0]])]});
            extrude(context, id + "F31", {"entities" : qUnion([Q0]), "depth" : 2.38 * mm});
        }
        {
            var Q0;
            Q0=makeQuery(id+"F5.opExtrude","SWEPT_BODY",BODY,{"disambiguationData":[OSD([sQuery(id+"F4.wireOp",EDGE,"E38.bottom"),sQuery(id+"F4.wireOp",EDGE,"E38.top"),sQuery(id+"F4.wireOp",EDGE,"E38.left"),sQuery(id+"F4.wireOp",EDGE,"E38.right"),sQuery(id+"F4.wireOp",EDGE,"E39.top"),sQuery(id+"F4.wireOp",EDGE,"E39.right"),sQuery(id+"F4.wireOp",EDGE,"E40.bottom"),sQuery(id+"F4.wireOp",EDGE,"E40.top"),sQuery(id+"F4.wireOp",EDGE,"E40.right"),sQuery(id+"F4.wireOp",EDGE,"E45.MirrorCS"),sQuery(id+"F4.wireOp",EDGE,"E46.MirrorCS"),sQuery(id+"F4.wireOp",EDGE,"E47.MirrorCS"),sQuery(id+"F4.wireOp",EDGE,"E48.MirrorCS"),sQuery(id+"F4.wireOp",EDGE,"E49.MirrorCS"),sQuery(id+"F4.wireOp",EDGE,"E50.bottom"),sQuery(id+"F4.wireOp",EDGE,"E51.top"),sQuery(id+"F4.wireOp",EDGE,"E51.right"),sQuery(id+"F4.wireOp",EDGE,"E52.MirrorCS"),sQuery(id+"F4.wireOp",EDGE,"E53.MirrorCS"),sQuery(id+"F4.wireOp",EDGE,"E54.top"),sQuery(id+"F4.wireOp",EDGE,"E54.left"),sQuery(id+"F4.wireOp",EDGE,"E55.MirrorCS"),sQuery(id+"F4.wireOp",EDGE,"E56.MirrorCS"),sQuery(id+"F4.wireOp",EDGE,"E57.top"),sQuery(id+"F4.wireOp",EDGE,"E57.right"),sQuery(id+"F4.wireOp",EDGE,"E58.MirrorCS"),sQuery(id+"F4.wireOp",EDGE,"E59.MirrorCS")])]});
            transform(context, id + "F32", {"entities" : qUnion([Q0]), "transformType" : TransformType.TRANSLATION_3D, "dx" : 0 * mm, "dy" : 0 * mm, "dz" : 0 * mm, "makeCopy" : true});
        }
        {
            var Q0;
            Q0=makeQuery(id+"F32.opPattern","COPY",BODY,{"derivedFrom":makeQuery(id+"F5.opExtrude","SWEPT_BODY",BODY,{"disambiguationData":[OSD([sQuery(id+"F4.wireOp",EDGE,"E38.bottom"),sQuery(id+"F4.wireOp",EDGE,"E38.top"),sQuery(id+"F4.wireOp",EDGE,"E38.left"),sQuery(id+"F4.wireOp",EDGE,"E38.right"),sQuery(id+"F4.wireOp",EDGE,"E39.top"),sQuery(id+"F4.wireOp",EDGE,"E39.right"),sQuery(id+"F4.wireOp",EDGE,"E40.bottom"),sQuery(id+"F4.wireOp",EDGE,"E40.top"),sQuery(id+"F4.wireOp",EDGE,"E40.right"),sQuery(id+"F4.wireOp",EDGE,"E45.MirrorCS"),sQuery(id+"F4.wireOp",EDGE,"E46.MirrorCS"),sQuery(id+"F4.wireOp",EDGE,"E47.MirrorCS"),sQuery(id+"F4.wireOp",EDGE,"E48.MirrorCS"),sQuery(id+"F4.wireOp",EDGE,"E49.MirrorCS"),sQuery(id+"F4.wireOp",EDGE,"E50.bottom"),sQuery(id+"F4.wireOp",EDGE,"E51.top"),sQuery(id+"F4.wireOp",EDGE,"E51.right"),sQuery(id+"F4.wireOp",EDGE,"E52.MirrorCS"),sQuery(id+"F4.wireOp",EDGE,"E53.MirrorCS"),sQuery(id+"F4.wireOp",EDGE,"E54.top"),sQuery(id+"F4.wireOp",EDGE,"E54.left"),sQuery(id+"F4.wireOp",EDGE,"E55.MirrorCS"),sQuery(id+"F4.wireOp",EDGE,"E56.MirrorCS"),sQuery(id+"F4.wireOp",EDGE,"E57.top"),sQuery(id+"F4.wireOp",EDGE,"E57.right"),sQuery(id+"F4.wireOp",EDGE,"E58.MirrorCS"),sQuery(id+"F4.wireOp",EDGE,"E59.MirrorCS")])]}),"instanceName":"1"});
            deleteBodies(context, id + "F33", {"entities" : qUnion([Q0])});
        }
        {
            var Q0;
            Q0=qCreatedBy(makeId("Right.planeOp"),FACE);
            var sketch = newSketch(context, id + "F34", { "sketchPlane" : qUnion([Q0])});
            skLineSegment(sketch, "E142.bottom", {"start": v(-244.06, 237.28) * mm, "end": v(-129.76, 237.28) * mm});
            skLineSegment(sketch, "E142.top", {"start": v(-244.06, 291.25) * mm, "end": v(-129.76, 291.25) * mm});
            skLineSegment(sketch, "E142.left", {"start": v(-244.06, 237.28) * mm, "end": v(-244.06, 291.25) * mm});
            skLineSegment(sketch, "E142.right", {"start": v(-129.76, 237.28) * mm, "end": v(-129.76, 291.25) * mm});
            skLineSegment(sketch, "E143.bottom", {"start": v(-244.06, 237.28) * mm, "end": v(-237.71, 237.28) * mm});
            skLineSegment(sketch, "E143.top", {"start": v(-244.06, 249.98) * mm, "end": v(-237.71, 249.98) * mm});
            skLineSegment(sketch, "E143.left", {"start": v(-244.06, 237.28) * mm, "end": v(-244.06, 249.98) * mm});
            skLineSegment(sketch, "E143.right", {"start": v(-237.71, 237.28) * mm, "end": v(-237.71, 249.98) * mm});
            skLineSegment(sketch, "E144.bottom", {"start": v(-244.06, 275.38) * mm, "end": v(-237.71, 275.38) * mm});
            skLineSegment(sketch, "E144.top", {"start": v(-244.06, 262.68) * mm, "end": v(-237.71, 262.68) * mm});
            skLineSegment(sketch, "E144.left", {"start": v(-244.06, 275.38) * mm, "end": v(-244.06, 262.68) * mm});
            skLineSegment(sketch, "E144.right", {"start": v(-237.71, 275.38) * mm, "end": v(-237.71, 262.68) * mm});
            skLineSegment(sketch, "E145.bottom", {"start": v(-231.36, 291.25) * mm, "end": v(-218.66, 291.25) * mm});
            skLineSegment(sketch, "E145.top", {"start": v(-231.36, 284.9) * mm, "end": v(-218.66, 284.9) * mm});
            skLineSegment(sketch, "E145.left", {"start": v(-231.36, 291.25) * mm, "end": v(-231.36, 284.9) * mm});
            skLineSegment(sketch, "E145.right", {"start": v(-218.66, 291.25) * mm, "end": v(-218.66, 284.9) * mm});
            skLineSegment(sketch, "E146.1.0.0", {"start": v(-205.96, 291.25) * mm, "end": v(-205.96, 284.9) * mm});
            skLineSegment(sketch, "E146.1.0.1", {"start": v(-193.26, 291.25) * mm, "end": v(-193.26, 284.9) * mm});
            skLineSegment(sketch, "E146.1.0.2", {"start": v(-205.96, 291.25) * mm, "end": v(-193.26, 291.25) * mm});
            skLineSegment(sketch, "E146.1.0.3", {"start": v(-205.96, 284.9) * mm, "end": v(-193.26, 284.9) * mm});
            skLineSegment(sketch, "E146.2.0.0", {"start": v(-180.56, 291.25) * mm, "end": v(-180.56, 284.9) * mm});
            skLineSegment(sketch, "E146.2.0.1", {"start": v(-167.86, 291.25) * mm, "end": v(-167.86, 284.9) * mm});
            skLineSegment(sketch, "E146.2.0.2", {"start": v(-180.56, 291.25) * mm, "end": v(-167.86, 291.25) * mm});
            skLineSegment(sketch, "E146.2.0.3", {"start": v(-180.56, 284.9) * mm, "end": v(-167.86, 284.9) * mm});
            skLineSegment(sketch, "E146.3.0.0", {"start": v(-155.16, 291.25) * mm, "end": v(-155.16, 284.9) * mm});
            skLineSegment(sketch, "E146.3.0.1", {"start": v(-142.46, 291.25) * mm, "end": v(-142.46, 284.9) * mm});
            skLineSegment(sketch, "E146.3.0.2", {"start": v(-155.16, 291.25) * mm, "end": v(-142.46, 291.25) * mm});
            skLineSegment(sketch, "E146.3.0.3", {"start": v(-155.16, 284.9) * mm, "end": v(-142.46, 284.9) * mm});
            skLineSegment(sketch, "E146.direction1", {"start": v(-244.06, 291.25) * mm, "end": v(-218.66, 291.25) * mm, "construction": true});
            skLineSegment(sketch, "E147", {"start": v(-186.91, 291.25) * mm, "end": v(-186.91, 237.28) * mm, "construction": true});
            skLineSegment(sketch, "E148.MirrorCS", {"start": v(-129.76, 262.68) * mm, "end": v(-136.11, 262.68) * mm});
            skLineSegment(sketch, "E149.MirrorCS", {"start": v(-129.76, 275.38) * mm, "end": v(-136.11, 275.38) * mm});
            skLineSegment(sketch, "E150.MirrorCS", {"start": v(-136.11, 275.38) * mm, "end": v(-136.11, 262.68) * mm});
            skLineSegment(sketch, "E151.MirrorCS", {"start": v(-129.76, 249.98) * mm, "end": v(-136.11, 249.98) * mm});
            skLineSegment(sketch, "E152.MirrorCS", {"start": v(-136.11, 237.28) * mm, "end": v(-136.11, 249.98) * mm});
            skSolve(sketch);
        }
        {
            var Q0;
            {var subQ6=sQuery(id+"F34.wireOp",EDGE,"E143.top");Q0=makeQuery(id+"F34.imprint","IMPRINT",FACE,{"disambiguationData":[TD([[makeQuery(id+"F34.imprint","IMPRINT",EDGE,{"derivedFrom":subQ6}),1.0]])]});}
            extrude(context, id + "F35", {"entities" : qUnion([Q0]), "depth" : 6.35 * mm});
        }
        {
            var Q0;
            Q0=qCreatedBy(makeId("Right.planeOp"),FACE);
            var sketch = newSketch(context, id + "F36", { "sketchPlane" : qUnion([Q0])});
            skLineSegment(sketch, "E153.bottom", {"start": v(-83.94, 241.82) * mm, "end": v(-7.74, 241.82) * mm});
            skLineSegment(sketch, "E153.top", {"start": v(-83.94, 295.8) * mm, "end": v(-7.74, 295.8) * mm});
            skLineSegment(sketch, "E153.left", {"start": v(-83.94, 241.82) * mm, "end": v(-83.94, 295.8) * mm});
            skLineSegment(sketch, "E153.right", {"start": v(-7.74, 241.82) * mm, "end": v(-7.74, 295.8) * mm});
            skLineSegment(sketch, "E154.bottom", {"start": v(-83.94, 295.8) * mm, "end": v(-77.59, 295.8) * mm});
            skLineSegment(sketch, "E154.top", {"start": v(-83.94, 279.92) * mm, "end": v(-77.59, 279.92) * mm});
            skLineSegment(sketch, "E154.left", {"start": v(-83.94, 295.8) * mm, "end": v(-83.94, 279.92) * mm});
            skLineSegment(sketch, "E154.right", {"start": v(-77.59, 295.8) * mm, "end": v(-77.59, 279.92) * mm});
            skLineSegment(sketch, "E155.bottom", {"start": v(-83.94, 254.52) * mm, "end": v(-77.59, 254.52) * mm});
            skLineSegment(sketch, "E155.top", {"start": v(-83.94, 267.22) * mm, "end": v(-77.59, 267.22) * mm});
            skLineSegment(sketch, "E155.left", {"start": v(-83.94, 254.52) * mm, "end": v(-83.94, 267.22) * mm});
            skLineSegment(sketch, "E155.right", {"start": v(-77.59, 254.52) * mm, "end": v(-77.59, 267.22) * mm});
            skLineSegment(sketch, "E156.bottom", {"start": v(-64.89, 295.8) * mm, "end": v(-52.19, 295.8) * mm});
            skLineSegment(sketch, "E156.top", {"start": v(-64.89, 289.44) * mm, "end": v(-52.19, 289.44) * mm});
            skLineSegment(sketch, "E156.left", {"start": v(-64.89, 295.8) * mm, "end": v(-64.89, 289.44) * mm});
            skLineSegment(sketch, "E156.right", {"start": v(-52.19, 295.8) * mm, "end": v(-52.19, 289.44) * mm});
            skLineSegment(sketch, "E157.1.0.0", {"start": v(-26.79, 295.8) * mm, "end": v(-26.79, 289.44) * mm});
            skLineSegment(sketch, "E157.1.0.1", {"start": v(-39.49, 289.44) * mm, "end": v(-26.79, 289.44) * mm});
            skLineSegment(sketch, "E157.1.0.2", {"start": v(-39.49, 295.8) * mm, "end": v(-39.49, 289.44) * mm});
            skLineSegment(sketch, "E157.direction1", {"start": v(-64.89, 289.44) * mm, "end": v(-39.49, 289.44) * mm, "construction": true});
            skLineSegment(sketch, "E158", {"start": v(-45.84, 241.82) * mm, "end": v(-45.84, 295.8) * mm, "construction": true});
            skLineSegment(sketch, "E159.MirrorCS", {"start": v(-7.74, 254.52) * mm, "end": v(-14.09, 254.52) * mm});
            skLineSegment(sketch, "E160.MirrorCS", {"start": v(-7.74, 267.22) * mm, "end": v(-14.09, 267.22) * mm});
            skLineSegment(sketch, "E161.MirrorCS", {"start": v(-7.74, 279.92) * mm, "end": v(-14.09, 279.92) * mm});
            skLineSegment(sketch, "E162.MirrorCS", {"start": v(-14.09, 295.8) * mm, "end": v(-14.09, 279.92) * mm});
            skLineSegment(sketch, "E163.MirrorCS", {"start": v(-14.09, 254.52) * mm, "end": v(-14.09, 267.22) * mm});
            skSolve(sketch);
        }
        {
            var Q0;
            {var subQ13=sQuery(id+"F36.wireOp",EDGE,"E153.bottom");Q0=makeQuery(id+"F36.imprint","IMPRINT",FACE,{"disambiguationData":[TD([[makeQuery(id+"F36.imprint","IMPRINT",EDGE,{"derivedFrom":subQ13}),1.0]])]});}
            extrude(context, id + "F37", {"entities" : qUnion([Q0]), "depth" : 6.35 * mm});
        }
        {
            var Q0;
            Q0=qCreatedBy(makeId("Right.planeOp"),FACE);
            var sketch = newSketch(context, id + "F38", { "sketchPlane" : qUnion([Q0])});
            skLineSegment(sketch, "E164.bottom", {"start": v(-505.29, 353.03) * mm, "end": v(-390.99, 353.03) * mm});
            skLineSegment(sketch, "E164.top", {"start": v(-505.29, 429.23) * mm, "end": v(-390.99, 429.23) * mm});
            skLineSegment(sketch, "E164.left", {"start": v(-505.29, 353.03) * mm, "end": v(-505.29, 429.23) * mm});
            skLineSegment(sketch, "E164.right", {"start": v(-390.99, 353.03) * mm, "end": v(-390.99, 429.23) * mm});
            skLineSegment(sketch, "E165.bottom", {"start": v(-505.29, 429.23) * mm, "end": v(-492.59, 429.23) * mm});
            skLineSegment(sketch, "E165.top", {"start": v(-505.29, 422.88) * mm, "end": v(-492.59, 422.88) * mm});
            skLineSegment(sketch, "E165.left", {"start": v(-505.29, 429.23) * mm, "end": v(-505.29, 422.88) * mm});
            skLineSegment(sketch, "E165.right", {"start": v(-492.59, 429.23) * mm, "end": v(-492.59, 422.88) * mm});
            skLineSegment(sketch, "E166", {"start": v(-448.14, 429.23) * mm, "end": v(-448.14, 353.03) * mm, "construction": true});
            skLineSegment(sketch, "E167.1.0.0", {"start": v(-467.19, 429.23) * mm, "end": v(-467.19, 422.88) * mm});
            skLineSegment(sketch, "E167.1.0.1", {"start": v(-479.89, 422.88) * mm, "end": v(-467.19, 422.88) * mm});
            skLineSegment(sketch, "E167.1.0.2", {"start": v(-479.89, 429.23) * mm, "end": v(-467.19, 429.23) * mm});
            skLineSegment(sketch, "E167.1.0.3", {"start": v(-479.89, 429.23) * mm, "end": v(-479.89, 422.88) * mm});
            skLineSegment(sketch, "E167.2.0.0", {"start": v(-441.79, 429.23) * mm, "end": v(-441.79, 422.88) * mm});
            skLineSegment(sketch, "E167.2.0.1", {"start": v(-454.49, 422.88) * mm, "end": v(-441.79, 422.88) * mm});
            skLineSegment(sketch, "E167.2.0.2", {"start": v(-454.49, 429.23) * mm, "end": v(-441.79, 429.23) * mm});
            skLineSegment(sketch, "E167.2.0.3", {"start": v(-454.49, 429.23) * mm, "end": v(-454.49, 422.88) * mm});
            skLineSegment(sketch, "E167.3.0.0", {"start": v(-416.39, 429.23) * mm, "end": v(-416.39, 422.88) * mm});
            skLineSegment(sketch, "E167.3.0.1", {"start": v(-429.09, 422.88) * mm, "end": v(-416.39, 422.88) * mm});
            skLineSegment(sketch, "E167.3.0.2", {"start": v(-429.09, 429.23) * mm, "end": v(-416.39, 429.23) * mm});
            skLineSegment(sketch, "E167.3.0.3", {"start": v(-429.09, 429.23) * mm, "end": v(-429.09, 422.88) * mm});
            skLineSegment(sketch, "E167.4.0.0", {"start": v(-390.99, 429.23) * mm, "end": v(-390.99, 422.88) * mm});
            skLineSegment(sketch, "E167.4.0.1", {"start": v(-403.69, 422.88) * mm, "end": v(-390.99, 422.88) * mm});
            skLineSegment(sketch, "E167.4.0.2", {"start": v(-403.69, 429.23) * mm, "end": v(-390.99, 429.23) * mm});
            skLineSegment(sketch, "E167.4.0.3", {"start": v(-403.69, 429.23) * mm, "end": v(-403.69, 422.88) * mm});
            skLineSegment(sketch, "E167.direction1", {"start": v(-505.29, 422.88) * mm, "end": v(-479.89, 422.88) * mm, "construction": true});
            skPoint(sketch, "E168.oppositeSnap0", {"position": v(-498.94, 422.88) * mm});
            skLineSegment(sketch, "E168.bottom", {"start": v(-505.29, 359.38) * mm, "end": v(-498.94, 359.38) * mm});
            skLineSegment(sketch, "E168.top", {"start": v(-505.29, 372.08) * mm, "end": v(-498.94, 372.08) * mm});
            skLineSegment(sketch, "E168.left", {"start": v(-505.29, 359.38) * mm, "end": v(-505.29, 372.08) * mm});
            skLineSegment(sketch, "E168.right", {"start": v(-498.94, 359.38) * mm, "end": v(-498.94, 372.08) * mm});
            skLineSegment(sketch, "E169.0.1.0", {"start": v(-498.94, 384.78) * mm, "end": v(-498.94, 397.48) * mm});
            skLineSegment(sketch, "E169.0.1.1", {"start": v(-505.29, 384.78) * mm, "end": v(-498.94, 384.78) * mm});
            skLineSegment(sketch, "E169.0.1.2", {"start": v(-505.29, 397.48) * mm, "end": v(-498.94, 397.48) * mm});
            skLineSegment(sketch, "E169.0.1.3", {"start": v(-505.29, 384.78) * mm, "end": v(-505.29, 397.48) * mm});
            skLineSegment(sketch, "E169.0.2.0", {"start": v(-498.94, 410.18) * mm, "end": v(-498.94, 422.88) * mm});
            skLineSegment(sketch, "E169.0.2.1", {"start": v(-505.29, 410.18) * mm, "end": v(-498.94, 410.18) * mm});
            skLineSegment(sketch, "E169.0.2.2", {"start": v(-505.29, 422.88) * mm, "end": v(-498.94, 422.88) * mm});
            skLineSegment(sketch, "E169.0.2.3", {"start": v(-505.29, 410.18) * mm, "end": v(-505.29, 422.88) * mm});
            skLineSegment(sketch, "E169.direction1", {"start": v(-505.29, 359.38) * mm, "end": v(-479.89, 359.38) * mm, "construction": true});
            skLineSegment(sketch, "E169.direction2", {"start": v(-505.29, 359.38) * mm, "end": v(-505.29, 384.78) * mm, "construction": true});
            skLineSegment(sketch, "E170", {"start": v(-505.29, 391.13) * mm, "end": v(-390.99, 391.13) * mm, "construction": true});
            skLineSegment(sketch, "E171.MirrorCS", {"start": v(-505.29, 359.38) * mm, "end": v(-492.59, 359.38) * mm});
            skLineSegment(sketch, "E172.MirrorCS", {"start": v(-479.89, 359.38) * mm, "end": v(-467.19, 359.38) * mm});
            skLineSegment(sketch, "E173.MirrorCS", {"start": v(-467.19, 353.03) * mm, "end": v(-467.19, 359.38) * mm});
            skLineSegment(sketch, "E174.MirrorCS", {"start": v(-479.89, 353.03) * mm, "end": v(-479.89, 359.38) * mm});
            skLineSegment(sketch, "E175.MirrorCS", {"start": v(-429.09, 359.38) * mm, "end": v(-416.39, 359.38) * mm});
            skLineSegment(sketch, "E176.MirrorCS", {"start": v(-492.59, 353.03) * mm, "end": v(-492.59, 359.38) * mm});
            skLineSegment(sketch, "E177.MirrorCS", {"start": v(-403.69, 359.38) * mm, "end": v(-390.99, 359.38) * mm});
            skLineSegment(sketch, "E178.MirrorCS", {"start": v(-416.39, 353.03) * mm, "end": v(-416.39, 359.38) * mm});
            skLineSegment(sketch, "E179.MirrorCS", {"start": v(-441.79, 353.03) * mm, "end": v(-441.79, 359.38) * mm});
            skLineSegment(sketch, "E180.MirrorCS", {"start": v(-429.09, 353.03) * mm, "end": v(-429.09, 359.38) * mm});
            skLineSegment(sketch, "E181.MirrorCS", {"start": v(-454.49, 359.38) * mm, "end": v(-441.79, 359.38) * mm});
            skLineSegment(sketch, "E182.MirrorCS", {"start": v(-448.14, 353.03) * mm, "end": v(-448.14, 429.23) * mm, "construction": true});
            skLineSegment(sketch, "E183.MirrorCS", {"start": v(-403.69, 353.03) * mm, "end": v(-403.69, 359.38) * mm});
            skLineSegment(sketch, "E184.MirrorCS", {"start": v(-454.49, 353.03) * mm, "end": v(-454.49, 359.38) * mm});
            skLineSegment(sketch, "E185.MirrorCS", {"start": v(-390.99, 384.78) * mm, "end": v(-397.34, 384.78) * mm});
            skLineSegment(sketch, "E186.MirrorCS", {"start": v(-397.34, 359.38) * mm, "end": v(-397.34, 372.08) * mm});
            skLineSegment(sketch, "E187.MirrorCS", {"start": v(-390.99, 397.48) * mm, "end": v(-397.34, 397.48) * mm});
            skLineSegment(sketch, "E188.MirrorCS", {"start": v(-390.99, 391.13) * mm, "end": v(-505.29, 391.13) * mm, "construction": true});
            skLineSegment(sketch, "E189.MirrorCS", {"start": v(-397.34, 384.78) * mm, "end": v(-397.34, 397.48) * mm});
            skLineSegment(sketch, "E190.MirrorCS", {"start": v(-390.99, 410.18) * mm, "end": v(-397.34, 410.18) * mm});
            skLineSegment(sketch, "E191.MirrorCS", {"start": v(-397.34, 410.18) * mm, "end": v(-397.34, 422.88) * mm});
            skLineSegment(sketch, "E192.MirrorCS", {"start": v(-390.99, 372.08) * mm, "end": v(-397.34, 372.08) * mm});
            skPoint(sketch, "E193.firstSnap0", {"position": v(-448.14, 359.38) * mm});
            skLineSegment(sketch, "E193.bottom", {"start": v(-448.14, 327.63) * mm, "end": v(-143.34, 327.63) * mm});
            skLineSegment(sketch, "E193.top", {"start": v(-448.14, 454.63) * mm, "end": v(-143.34, 454.63) * mm});
            skLineSegment(sketch, "E193.left", {"start": v(-448.14, 327.63) * mm, "end": v(-448.14, 454.63) * mm});
            skLineSegment(sketch, "E193.right", {"start": v(-143.34, 327.63) * mm, "end": v(-143.34, 454.63) * mm});
            skLineSegment(sketch, "E194", {"start": v(-295.74, 454.63) * mm, "end": v(-295.74, 327.63) * mm, "construction": true});
            skLineSegment(sketch, "E195.MirrorCS", {"start": v(-149.69, 429.23) * mm, "end": v(-149.69, 422.88) * mm});
            skLineSegment(sketch, "E196.MirrorCS", {"start": v(-187.79, 429.23) * mm, "end": v(-187.79, 422.88) * mm});
            skLineSegment(sketch, "E197.MirrorCS", {"start": v(-175.09, 429.23) * mm, "end": v(-175.09, 422.88) * mm});
            skLineSegment(sketch, "E198.MirrorCS", {"start": v(-162.39, 429.23) * mm, "end": v(-162.39, 422.88) * mm});
            skLineSegment(sketch, "E199.MirrorCS", {"start": v(-200.49, 429.23) * mm, "end": v(-200.49, 422.88) * mm});
            skLineSegment(sketch, "E200.MirrorCS", {"start": v(-187.79, 422.88) * mm, "end": v(-200.49, 422.88) * mm});
            skLineSegment(sketch, "E201.MirrorCS", {"start": v(-187.79, 353.03) * mm, "end": v(-187.79, 359.38) * mm});
            skLineSegment(sketch, "E202.MirrorCS", {"start": v(-187.79, 359.38) * mm, "end": v(-200.49, 359.38) * mm});
            skLineSegment(sketch, "E203.MirrorCS", {"start": v(-200.49, 410.18) * mm, "end": v(-194.14, 410.18) * mm});
            skLineSegment(sketch, "E204.MirrorCS", {"start": v(-200.49, 397.48) * mm, "end": v(-194.14, 397.48) * mm});
            skLineSegment(sketch, "E205.MirrorCS", {"start": v(-200.49, 384.78) * mm, "end": v(-194.14, 384.78) * mm});
            skLineSegment(sketch, "E206.MirrorCS", {"start": v(-175.09, 353.03) * mm, "end": v(-175.09, 359.38) * mm});
            skLineSegment(sketch, "E207.MirrorCS", {"start": v(-162.39, 353.03) * mm, "end": v(-162.39, 359.38) * mm});
            skLineSegment(sketch, "E208.MirrorCS", {"start": v(-149.69, 353.03) * mm, "end": v(-149.69, 359.38) * mm});
            skLineSegment(sketch, "E209.MirrorCS", {"start": v(-200.49, 372.08) * mm, "end": v(-194.14, 372.08) * mm});
            skLineSegment(sketch, "E210.MirrorCS", {"start": v(-194.14, 384.78) * mm, "end": v(-194.14, 397.48) * mm});
            skLineSegment(sketch, "E211.MirrorCS", {"start": v(-187.79, 429.23) * mm, "end": v(-200.49, 429.23) * mm});
            skLineSegment(sketch, "E212.MirrorCS", {"start": v(-162.39, 359.38) * mm, "end": v(-175.09, 359.38) * mm});
            skLineSegment(sketch, "E213.MirrorCS", {"start": v(-194.14, 359.38) * mm, "end": v(-194.14, 372.08) * mm});
            skLineSegment(sketch, "E214.MirrorCS", {"start": v(-194.14, 410.18) * mm, "end": v(-194.14, 422.88) * mm});
            skLineSegment(sketch, "E215.MirrorCS", {"start": v(-200.49, 353.03) * mm, "end": v(-200.49, 429.23) * mm});
            skLineSegment(sketch, "E216.MirrorCS", {"start": v(-162.39, 429.23) * mm, "end": v(-175.09, 429.23) * mm});
            skLineSegment(sketch, "E217.MirrorCS", {"start": v(-162.39, 422.88) * mm, "end": v(-175.09, 422.88) * mm});
            skLineSegment(sketch, "E218.MirrorCS", {"start": v(-136.99, 359.38) * mm, "end": v(-149.69, 359.38) * mm});
            skLineSegment(sketch, "E219.MirrorCS", {"start": v(-143.34, 422.88) * mm, "end": v(-149.69, 422.88) * mm});
            skLineSegment(sketch, "E220.MirrorCS", {"start": v(-86.19, 353.03) * mm, "end": v(-200.49, 353.03) * mm});
            skLineSegment(sketch, "E221", {"start": v(-149.69, 429.23) * mm, "end": v(-143.34, 429.23) * mm});
            skLineSegment(sketch, "E222", {"start": v(-143.34, 429.23) * mm, "end": v(-143.34, 422.88) * mm});
            skPoint(sketch, "E223.orphan", {"position": v(-136.99, 422.88) * mm});
            skSolve(sketch);
        }
        {
            var Q0;
            {var subQ16=sQuery(id+"F38.wireOp",EDGE,"E167.3.0.2");Q0=makeQuery(id+"F38.imprint","IMPRINT",FACE,{"disambiguationData":[TD([[makeQuery(id+"F38.imprint","IMPRINT",EDGE,{"derivedFrom":subQ16}),1.0]])]});}
            var Q1;
            {var subQ7=sQuery(id+"F38.wireOp",EDGE,"E167.2.0.0");Q1=makeQuery(id+"F38.imprint","IMPRINT",FACE,{"disambiguationData":[TD([[makeQuery(id+"F38.imprint","IMPRINT",EDGE,{"derivedFrom":subQ7}),1.0]])]});}
            extrude(context, id + "F39", {"entities" : qUnion([Q0, Q1]), "depth" : 6.35 * mm});
        }
        {
            var Q0;
            Q0=qCreatedBy(makeId("Right.planeOp"),FACE);
            var sketch = newSketch(context, id + "F40", { "sketchPlane" : qUnion([Q0])});
            skLineSegment(sketch, "E224.left", {"start": v(-684.86, 283.5) * mm, "end": v(-684.86, 410.5) * mm});
            skLineSegment(sketch, "E225.bottom", {"start": v(-684.86, 410.5) * mm, "end": v(-691.2, 410.5) * mm});
            skLineSegment(sketch, "E225.top", {"start": v(-684.86, 404.14) * mm, "end": v(-691.2, 404.14) * mm});
            skLineSegment(sketch, "E225.left", {"start": v(-684.86, 410.5) * mm, "end": v(-684.86, 404.14) * mm});
            skLineSegment(sketch, "E225.right", {"start": v(-691.2, 410.5) * mm, "end": v(-691.2, 404.14) * mm});
            skLineSegment(sketch, "E226.bottom", {"start": v(-684.86, 391.44) * mm, "end": v(-691.2, 391.44) * mm});
            skLineSegment(sketch, "E226.top", {"start": v(-684.86, 378.74) * mm, "end": v(-691.2, 378.74) * mm});
            skLineSegment(sketch, "E226.left", {"start": v(-684.86, 391.44) * mm, "end": v(-684.86, 378.74) * mm});
            skLineSegment(sketch, "E226.right", {"start": v(-691.2, 391.44) * mm, "end": v(-691.2, 378.74) * mm});
            skLineSegment(sketch, "E227.0.1.0", {"start": v(-691.2, 366.04) * mm, "end": v(-691.2, 353.34) * mm});
            skLineSegment(sketch, "E227.0.1.1", {"start": v(-684.86, 353.34) * mm, "end": v(-691.2, 353.34) * mm});
            skLineSegment(sketch, "E227.0.1.2", {"start": v(-684.86, 366.04) * mm, "end": v(-691.2, 366.04) * mm});
            skLineSegment(sketch, "E227.0.2.0", {"start": v(-691.2, 340.64) * mm, "end": v(-691.2, 327.94) * mm});
            skLineSegment(sketch, "E227.0.2.1", {"start": v(-684.86, 327.94) * mm, "end": v(-691.2, 327.94) * mm});
            skLineSegment(sketch, "E227.0.2.2", {"start": v(-684.86, 340.64) * mm, "end": v(-691.2, 340.64) * mm});
            skLineSegment(sketch, "E227.0.3.0", {"start": v(-691.2, 315.24) * mm, "end": v(-691.2, 302.54) * mm});
            skLineSegment(sketch, "E227.0.3.1", {"start": v(-684.86, 302.54) * mm, "end": v(-691.2, 302.54) * mm});
            skLineSegment(sketch, "E227.0.3.2", {"start": v(-684.86, 315.24) * mm, "end": v(-691.2, 315.24) * mm});
            skLineSegment(sketch, "E227.direction1", {"start": v(-691.2, 378.74) * mm, "end": v(-665.8, 378.74) * mm, "construction": true});
            skLineSegment(sketch, "E227.direction2", {"start": v(-691.2, 378.74) * mm, "end": v(-691.2, 353.34) * mm, "construction": true});
            skLineSegment(sketch, "E228.MirrorCS", {"start": v(-684.86, 289.84) * mm, "end": v(-691.2, 289.84) * mm});
            skLineSegment(sketch, "E229.MirrorCS", {"start": v(-691.2, 283.5) * mm, "end": v(-691.2, 289.84) * mm});
            skLineSegment(sketch, "E230.left", {"start": v(-691.2, 388.27) * mm, "end": v(-691.2, 381.92) * mm});
            skLineSegment(sketch, "E231.direction1", {"start": v(-691.2, 353.34) * mm, "end": v(-716.6, 353.34) * mm, "construction": true});
            skLineSegment(sketch, "E232.MirrorCS", {"start": v(-691.2, 315.24) * mm, "end": v(-691.2, 340.64) * mm, "construction": true});
            skLineSegment(sketch, "E233", {"start": v(-691.2, 312.07) * mm, "end": v(-691.2, 305.72) * mm});
            skLineSegment(sketch, "E234.bottom", {"start": v(-703.9, 388.27) * mm, "end": v(-716.6, 388.27) * mm});
            skLineSegment(sketch, "E234.top", {"start": v(-703.9, 381.92) * mm, "end": v(-716.6, 381.92) * mm});
            skLineSegment(sketch, "E234.left", {"start": v(-703.9, 388.27) * mm, "end": v(-703.9, 381.92) * mm});
            skLineSegment(sketch, "E234.right", {"start": v(-716.6, 388.27) * mm, "end": v(-716.6, 381.92) * mm});
            skLineSegment(sketch, "E235.1.0.0", {"start": v(-729.3, 388.27) * mm, "end": v(-729.3, 381.92) * mm});
            skLineSegment(sketch, "E235.1.0.1", {"start": v(-742, 388.27) * mm, "end": v(-742, 381.92) * mm});
            skLineSegment(sketch, "E235.1.0.2", {"start": v(-729.3, 381.92) * mm, "end": v(-742, 381.92) * mm});
            skLineSegment(sketch, "E235.1.0.3", {"start": v(-729.3, 388.27) * mm, "end": v(-742, 388.27) * mm});
            skLineSegment(sketch, "E235.direction1", {"start": v(-716.6, 381.92) * mm, "end": v(-742, 381.92) * mm, "construction": true});
            skLineSegment(sketch, "E236.MirrorCS", {"start": v(-729.3, 312.07) * mm, "end": v(-742, 312.07) * mm});
            skLineSegment(sketch, "E237.MirrorCS", {"start": v(-742, 305.72) * mm, "end": v(-742, 312.07) * mm});
            skLineSegment(sketch, "E238.MirrorCS", {"start": v(-716.6, 312.07) * mm, "end": v(-742, 312.07) * mm, "construction": true});
            skLineSegment(sketch, "E239.MirrorCS", {"start": v(-716.6, 305.72) * mm, "end": v(-716.6, 312.07) * mm});
            skLineSegment(sketch, "E240.MirrorCS", {"start": v(-703.9, 305.72) * mm, "end": v(-703.9, 312.07) * mm});
            skLineSegment(sketch, "E241.MirrorCS", {"start": v(-703.9, 312.07) * mm, "end": v(-716.6, 312.07) * mm});
            skLineSegment(sketch, "E242.MirrorCS", {"start": v(-703.9, 305.72) * mm, "end": v(-716.6, 305.72) * mm});
            skLineSegment(sketch, "E243.MirrorCS", {"start": v(-729.3, 305.72) * mm, "end": v(-729.3, 312.07) * mm});
            skLineSegment(sketch, "E244.MirrorCS", {"start": v(-729.3, 305.72) * mm, "end": v(-742, 305.72) * mm});
            skLineSegment(sketch, "E245.bottom", {"start": v(-684.86, 410.5) * mm, "end": v(-1065.86, 410.5) * mm});
            skLineSegment(sketch, "E245.top", {"start": v(-684.86, 283.5) * mm, "end": v(-1065.86, 283.5) * mm});
            skLineSegment(sketch, "E245.left", {"start": v(-684.86, 410.5) * mm, "end": v(-684.86, 283.5) * mm});
            skLineSegment(sketch, "E245.right", {"start": v(-1065.86, 410.5) * mm, "end": v(-1065.86, 283.5) * mm});
            skLineSegment(sketch, "E246.bottom", {"start": v(-1065.86, 385.1) * mm, "end": v(-1008.7, 385.1) * mm});
            skLineSegment(sketch, "E246.top", {"start": v(-1065.86, 308.9) * mm, "end": v(-1008.7, 308.9) * mm});
            skLineSegment(sketch, "E246.left", {"start": v(-1065.86, 385.1) * mm, "end": v(-1065.86, 308.9) * mm});
            skLineSegment(sketch, "E246.right", {"start": v(-1008.7, 385.1) * mm, "end": v(-1008.7, 308.9) * mm});
            skLineSegment(sketch, "E247.bottom", {"start": v(-1008.7, 385.1) * mm, "end": v(-1015.06, 385.1) * mm});
            skLineSegment(sketch, "E247.top", {"start": v(-1008.7, 366.04) * mm, "end": v(-1015.06, 366.04) * mm});
            skLineSegment(sketch, "E247.left", {"start": v(-1008.7, 385.1) * mm, "end": v(-1008.7, 366.04) * mm});
            skLineSegment(sketch, "E247.right", {"start": v(-1015.06, 385.1) * mm, "end": v(-1015.06, 366.04) * mm});
            skLineSegment(sketch, "E248.bottom", {"start": v(-1008.7, 353.34) * mm, "end": v(-1015.06, 353.34) * mm});
            skLineSegment(sketch, "E248.top", {"start": v(-1008.7, 340.64) * mm, "end": v(-1015.06, 340.64) * mm});
            skLineSegment(sketch, "E248.left", {"start": v(-1008.7, 353.34) * mm, "end": v(-1008.7, 340.64) * mm});
            skLineSegment(sketch, "E248.right", {"start": v(-1015.06, 353.34) * mm, "end": v(-1015.06, 340.64) * mm});
            skLineSegment(sketch, "E249.bottom", {"start": v(-1008.7, 385.1) * mm, "end": v(-1021.4, 385.1) * mm});
            skLineSegment(sketch, "E249.top", {"start": v(-1008.7, 378.74) * mm, "end": v(-1021.4, 378.74) * mm});
            skLineSegment(sketch, "E249.left", {"start": v(-1008.7, 385.1) * mm, "end": v(-1008.7, 378.74) * mm});
            skLineSegment(sketch, "E249.right", {"start": v(-1021.4, 385.1) * mm, "end": v(-1021.4, 378.74) * mm});
            skLineSegment(sketch, "E250.bottom", {"start": v(-1034.1, 385.1) * mm, "end": v(-1046.8, 385.1) * mm});
            skLineSegment(sketch, "E250.top", {"start": v(-1034.1, 378.74) * mm, "end": v(-1046.8, 378.74) * mm});
            skLineSegment(sketch, "E250.left", {"start": v(-1034.1, 385.1) * mm, "end": v(-1034.1, 378.74) * mm});
            skLineSegment(sketch, "E250.right", {"start": v(-1046.8, 385.1) * mm, "end": v(-1046.8, 378.74) * mm});
            skLineSegment(sketch, "E251.bottom", {"start": v(-1065.86, 385.1) * mm, "end": v(-1059.5, 385.1) * mm});
            skLineSegment(sketch, "E251.top", {"start": v(-1065.86, 378.74) * mm, "end": v(-1059.5, 378.74) * mm});
            skLineSegment(sketch, "E251.left", {"start": v(-1065.86, 385.1) * mm, "end": v(-1065.86, 378.74) * mm});
            skLineSegment(sketch, "E251.right", {"start": v(-1059.5, 385.1) * mm, "end": v(-1059.5, 378.74) * mm});
            skLineSegment(sketch, "E252", {"start": v(-1008.7, 347) * mm, "end": v(-1065.86, 347) * mm, "construction": true});
            skLineSegment(sketch, "E253.MirrorCS", {"start": v(-1034.1, 308.9) * mm, "end": v(-1034.1, 315.24) * mm});
            skLineSegment(sketch, "E254.MirrorCS", {"start": v(-1015.06, 308.9) * mm, "end": v(-1015.06, 327.94) * mm});
            skLineSegment(sketch, "E255.MirrorCS", {"start": v(-1046.8, 308.9) * mm, "end": v(-1046.8, 315.24) * mm});
            skLineSegment(sketch, "E256.MirrorCS", {"start": v(-1021.4, 308.9) * mm, "end": v(-1021.4, 315.24) * mm});
            skLineSegment(sketch, "E257.MirrorCS", {"start": v(-1034.1, 315.24) * mm, "end": v(-1046.8, 315.24) * mm});
            skLineSegment(sketch, "E258.MirrorCS", {"start": v(-1008.7, 315.24) * mm, "end": v(-1021.4, 315.24) * mm});
            skLineSegment(sketch, "E259.MirrorCS", {"start": v(-1065.86, 315.24) * mm, "end": v(-1059.5, 315.24) * mm});
            skLineSegment(sketch, "E260.MirrorCS", {"start": v(-1059.5, 308.9) * mm, "end": v(-1059.5, 315.24) * mm});
            skLineSegment(sketch, "E261.MirrorCS", {"start": v(-1008.7, 327.94) * mm, "end": v(-1015.06, 327.94) * mm});
            skLineSegment(sketch, "E262.bottom", {"start": v(-1062.68, 347) * mm, "end": v(-1069.03, 347) * mm});
            skLineSegment(sketch, "E262.top", {"start": v(-1062.68, 359.7) * mm, "end": v(-1069.03, 359.7) * mm});
            skLineSegment(sketch, "E262.left", {"start": v(-1062.68, 347) * mm, "end": v(-1062.68, 359.7) * mm});
            skLineSegment(sketch, "E262.right", {"start": v(-1069.03, 347) * mm, "end": v(-1069.03, 359.7) * mm});
            skLineSegment(sketch, "E263.MirrorCS", {"start": v(-1062.68, 334.3) * mm, "end": v(-1069.03, 334.3) * mm});
            skLineSegment(sketch, "E264.MirrorCS", {"start": v(-1062.68, 347) * mm, "end": v(-1062.68, 334.3) * mm});
            skLineSegment(sketch, "E265", {"start": v(-1065.86, 359.7) * mm, "end": v(-1008.7, 359.7) * mm, "construction": true});
            skLineSegment(sketch, "E266", {"start": v(-1065.86, 334.3) * mm, "end": v(-1008.7, 334.3) * mm, "construction": true});
            skLineSegment(sketch, "E267", {"start": v(-1069.03, 347) * mm, "end": v(-1069.03, 334.3) * mm});
            skLineSegment(sketch, "E268.MirrorCS", {"start": v(-1065.86, 258.1) * mm, "end": v(-1065.86, 385.1) * mm});
            skLineSegment(sketch, "E269.MirrorCS", {"start": v(-1069.03, 321.6) * mm, "end": v(-1069.03, 334.3) * mm});
            skLineSegment(sketch, "E270.MirrorCS", {"start": v(-1069.03, 321.6) * mm, "end": v(-1069.03, 308.9) * mm});
            skLineSegment(sketch, "E271.MirrorCS", {"start": v(-1062.68, 308.9) * mm, "end": v(-1069.03, 308.9) * mm});
            skLineSegment(sketch, "E272.MirrorCS", {"start": v(-1065.86, 308.9) * mm, "end": v(-1008.7, 308.9) * mm, "construction": true});
            skLineSegment(sketch, "E273.MirrorCS", {"start": v(-1008.7, 321.6) * mm, "end": v(-1065.86, 321.6) * mm, "construction": true});
            skLineSegment(sketch, "E274.MirrorCS", {"start": v(-1062.68, 321.6) * mm, "end": v(-1062.68, 334.3) * mm});
            skLineSegment(sketch, "E275.MirrorCS", {"start": v(-1062.68, 321.6) * mm, "end": v(-1069.03, 321.6) * mm});
            skLineSegment(sketch, "E276.MirrorCS", {"start": v(-1065.86, 283.5) * mm, "end": v(-1065.86, 359.7) * mm});
            skLineSegment(sketch, "E277.MirrorCS", {"start": v(-1062.68, 321.6) * mm, "end": v(-1062.68, 308.9) * mm});
            skLineSegment(sketch, "E278.MirrorCS", {"start": v(-1065.86, 308.9) * mm, "end": v(-1065.86, 435.9) * mm});
            skLineSegment(sketch, "E279.MirrorCS", {"start": v(-1065.86, 435.9) * mm, "end": v(-1065.86, 359.7) * mm});
            skLineSegment(sketch, "E280.MirrorCS", {"start": v(-1065.86, 461.3) * mm, "end": v(-1065.86, 334.3) * mm});
            skLineSegment(sketch, "E281.MirrorCS", {"start": v(-1062.68, 372.4) * mm, "end": v(-1069.03, 372.4) * mm});
            skLineSegment(sketch, "E282.MirrorCS", {"start": v(-1069.03, 372.4) * mm, "end": v(-1069.03, 359.7) * mm});
            skLineSegment(sketch, "E283.MirrorCS", {"start": v(-1065.86, 334.3) * mm, "end": v(-1065.86, 410.5) * mm});
            skLineSegment(sketch, "E284.MirrorCS", {"start": v(-1069.03, 372.4) * mm, "end": v(-1069.03, 385.1) * mm});
            skLineSegment(sketch, "E285.MirrorCS", {"start": v(-1008.7, 372.4) * mm, "end": v(-1065.86, 372.4) * mm, "construction": true});
            skLineSegment(sketch, "E286.MirrorCS", {"start": v(-1062.68, 372.4) * mm, "end": v(-1062.68, 359.7) * mm});
            skLineSegment(sketch, "E287.MirrorCS", {"start": v(-1062.68, 372.4) * mm, "end": v(-1062.68, 385.1) * mm});
            skLineSegment(sketch, "E288.MirrorCS", {"start": v(-1062.68, 385.1) * mm, "end": v(-1069.03, 385.1) * mm});
            skSolve(sketch);
        }
        {
            var Q0;
            {var subQ15=sQuery(id+"F40.wireOp",EDGE,"E225.top");Q0=makeQuery(id+"F40.imprint","IMPRINT",FACE,{"disambiguationData":[TD([[makeQuery(id+"F40.imprint","IMPRINT",EDGE,{"derivedFrom":subQ15}),1.0]])]});}
            var Q1;
            {var subQ13=sQuery(id+"F40.wireOp",EDGE,"E247.top");Q1=makeQuery(id+"F40.imprint","IMPRINT",FACE,{"disambiguationData":[TD([[makeQuery(id+"F40.imprint","IMPRINT",EDGE,{"derivedFrom":subQ13}),1.0]])]});}
            var Q2;
            {var subQ5=sQuery(id+"F40.wireOp",EDGE,"E262.left");Q2=makeQuery(id+"F40.imprint","IMPRINT",FACE,{"disambiguationData":[TD([[makeQuery(id+"F40.imprint","IMPRINT",EDGE,{"derivedFrom":subQ5}),1.0]])]});}
            var Q3;
            {var subQ5=sQuery(id+"F40.wireOp",EDGE,"E262.right");Q3=makeQuery(id+"F40.imprint","IMPRINT",FACE,{"disambiguationData":[TD([[makeQuery(id+"F40.imprint","IMPRINT",EDGE,{"derivedFrom":subQ5}),-1.0]])]});}
            var Q4;
            {var subQ0=sQuery(id+"F40.wireOp",EDGE,"E274.MirrorCS");Q4=makeQuery(id+"F40.imprint","IMPRINT",FACE,{"disambiguationData":[TD([[makeQuery(id+"F40.imprint","IMPRINT",EDGE,{"derivedFrom":subQ0}),1.0]])]});}
            var Q5;
            {var subQ0=sQuery(id+"F40.wireOp",EDGE,"E269.MirrorCS");Q5=makeQuery(id+"F40.imprint","IMPRINT",FACE,{"disambiguationData":[TD([[makeQuery(id+"F40.imprint","IMPRINT",EDGE,{"derivedFrom":subQ0}),-1.0]])]});}
            var Q6;
            {var subQ0=sQuery(id+"F40.wireOp",EDGE,"E278.MirrorCS");var subQ1=sQuery(id+"F40.wireOp",EDGE,"E259.MirrorCS");var subQ2=makeQuery(id+"F40.imprint","INTERSECT",VERTEX,{"derivedFrom":[subQ1,subQ0]});Q6=makeQuery(id+"F40.imprint","IMPRINT",FACE,{"disambiguationData":[TD([[makeQuery(id+"F40.imprint","IMPRINT",EDGE,{"disambiguationData":[TD([[subQ2,-1.0]])],"derivedFrom":subQ1}),1.0]])]});}
            var Q7;
            {var subQ0=sQuery(id+"F40.wireOp",EDGE,"E283.MirrorCS");var subQ1=sQuery(id+"F40.wireOp",EDGE,"E251.top");var subQ2=makeQuery(id+"F40.imprint","INTERSECT",VERTEX,{"derivedFrom":[subQ1,subQ0]});Q7=makeQuery(id+"F40.imprint","IMPRINT",FACE,{"disambiguationData":[TD([[makeQuery(id+"F40.imprint","IMPRINT",EDGE,{"disambiguationData":[TD([[subQ2,-1.0]])],"derivedFrom":subQ1}),-1.0]])]});}
            extrude(context, id + "F41", {"entities" : qUnion([Q0, Q1, Q2, Q3, Q4, Q5, Q6, Q7]), "depth" : 6.35 * mm});
        }
        {
            var Q0;
            Q0=makeQuery(id+"F3.opExtrude","CAP_FACE",FACE,{"disambiguationData":[OSD([sQuery(id+"F2.wireOp",EDGE,"E24.bottom"),sQuery(id+"F2.wireOp",EDGE,"E24.top"),sQuery(id+"F2.wireOp",EDGE,"E24.left"),sQuery(id+"F2.wireOp",EDGE,"E24.right"),sQuery(id+"F2.wireOp",EDGE,"E26.bottom"),sQuery(id+"F2.wireOp",EDGE,"E26.top"),sQuery(id+"F2.wireOp",EDGE,"E26.left"),sQuery(id+"F2.wireOp",EDGE,"E26.right"),sQuery(id+"F2.wireOp",EDGE,"E27.bottom"),sQuery(id+"F2.wireOp",EDGE,"E27.top"),sQuery(id+"F2.wireOp",EDGE,"E27.left"),sQuery(id+"F2.wireOp",EDGE,"E27.right"),sQuery(id+"F2.wireOp",EDGE,"E28.bottom"),sQuery(id+"F2.wireOp",EDGE,"E28.top"),sQuery(id+"F2.wireOp",EDGE,"E28.left"),sQuery(id+"F2.wireOp",EDGE,"E28.right"),sQuery(id+"F2.wireOp",EDGE,"E30.MirrorCS"),sQuery(id+"F2.wireOp",EDGE,"E31.MirrorCS"),sQuery(id+"F2.wireOp",EDGE,"E32.MirrorCS"),sQuery(id+"F2.wireOp",EDGE,"E33.MirrorCS"),sQuery(id+"F2.wireOp",EDGE,"E34.MirrorCS"),sQuery(id+"F2.wireOp",EDGE,"E35.MirrorCS"),sQuery(id+"F2.wireOp",EDGE,"E36.MirrorCS"),sQuery(id+"F2.wireOp",EDGE,"E37.MirrorCS")])],"isStart":true});
            var sketch = newSketch(context, id + "F42", { "sketchPlane" : qUnion([Q0])});
            skLineSegment(sketch, "E289.bottom", {"start": v(-350.78, 101.6) * mm, "end": v(-198.38, 101.6) * mm});
            skLineSegment(sketch, "E289.top", {"start": v(-350.78, 63.5) * mm, "end": v(-198.38, 63.5) * mm});
            skLineSegment(sketch, "E289.left", {"start": v(-350.78, 101.6) * mm, "end": v(-350.78, 63.5) * mm});
            skLineSegment(sketch, "E289.right", {"start": v(-198.38, 101.6) * mm, "end": v(-198.38, 63.5) * mm});
            skSolve(sketch);
        }
        {
            var Q0;
            Q0=makeQuery(id+"F42.imprint","IMPRINT",FACE,{"disambiguationData":[TD([[makeQuery(id+"F42.imprint","IMPRINT",EDGE,{"derivedFrom":sQuery(id+"F42.wireOp",EDGE,"E289.bottom")}),1.0]])]});
            extrude(context, id + "F43", {"entities" : qUnion([Q0]), "operationType" : NewBodyOperationType.REMOVE, "endBound" : BoundingType.UP_TO_NEXT, "oppositeDirection" : true, "depth" : 25.4 * mm});
        }
        {
            var Q0;
            Q0=makeQuery(id+"F1.opExtrude","CAP_FACE",FACE,{"disambiguationData":[OSD([sQuery(id+"F0.wireOp",EDGE,"E0.bottom"),sQuery(id+"F0.wireOp",EDGE,"E0.top"),sQuery(id+"F0.wireOp",EDGE,"E0.left"),sQuery(id+"F0.wireOp",EDGE,"E0.right"),sQuery(id+"F0.wireOp",EDGE,"E11.1.0.0"),sQuery(id+"F0.wireOp",EDGE,"E11.1.0.1"),sQuery(id+"F0.wireOp",EDGE,"E11.1.0.2"),sQuery(id+"F0.wireOp",EDGE,"E11.1.0.3"),sQuery(id+"F0.wireOp",EDGE,"E11.1.0.4"),sQuery(id+"F0.wireOp",EDGE,"E11.1.0.5"),sQuery(id+"F0.wireOp",EDGE,"E11.1.0.6"),sQuery(id+"F0.wireOp",EDGE,"E11.1.0.7"),sQuery(id+"F0.wireOp",EDGE,"E11.2.0.0"),sQuery(id+"F0.wireOp",EDGE,"E11.2.0.1"),sQuery(id+"F0.wireOp",EDGE,"E11.2.0.2"),sQuery(id+"F0.wireOp",EDGE,"E11.2.0.3"),sQuery(id+"F0.wireOp",EDGE,"E11.2.0.4"),sQuery(id+"F0.wireOp",EDGE,"E11.2.0.5"),sQuery(id+"F0.wireOp",EDGE,"E11.2.0.6"),sQuery(id+"F0.wireOp",EDGE,"E11.2.0.7"),sQuery(id+"F0.wireOp",EDGE,"E12.0.0.1"),sQuery(id+"F0.wireOp",EDGE,"E12.3.0.1"),sQuery(id+"F0.wireOp",EDGE,"E12.6.0.1"),sQuery(id+"F0.wireOp",EDGE,"E12.9.0.1"),sQuery(id+"F0.wireOp",EDGE,"E12.12.0.1"),sQuery(id+"F0.wireOp",EDGE,"E12.15.0.1"),sQuery(id+"F0.wireOp",EDGE,"E12.18.0.1"),sQuery(id+"F0.wireOp",EDGE,"E12.21.0.1"),sQuery(id+"F0.wireOp",EDGE,"E12.0.1.1"),sQuery(id+"F0.wireOp",EDGE,"E12.3.1.1"),sQuery(id+"F0.wireOp",EDGE,"E12.6.1.1"),sQuery(id+"F0.wireOp",EDGE,"E12.9.1.1"),sQuery(id+"F0.wireOp",EDGE,"E12.12.1.1"),sQuery(id+"F0.wireOp",EDGE,"E12.15.1.1"),sQuery(id+"F0.wireOp",EDGE,"E12.18.1.1"),sQuery(id+"F0.wireOp",EDGE,"E12.21.1.1"),sQuery(id+"F0.wireOp",EDGE,"E3"),sQuery(id+"F0.wireOp",EDGE,"E6.MirrorCS"),sQuery(id+"F0.wireOp",EDGE,"E5.MirrorCS"),sQuery(id+"F0.wireOp",EDGE,"E10.MirrorCS"),sQuery(id+"F0.wireOp",EDGE,"E9.MirrorCS"),sQuery(id+"F0.wireOp",EDGE,"E8.MirrorCS"),sQuery(id+"F0.wireOp",EDGE,"E7.MirrorCS"),sQuery(id+"F0.wireOp",EDGE,"E4"),sQuery(id+"F0.wireOp",EDGE,"E13.bottom"),sQuery(id+"F0.wireOp",EDGE,"E13.top"),sQuery(id+"F0.wireOp",EDGE,"E13.left"),sQuery(id+"F0.wireOp",EDGE,"E13.right"),sQuery(id+"F0.wireOp",EDGE,"E14.0.1.0"),sQuery(id+"F0.wireOp",EDGE,"E14.0.1.1"),sQuery(id+"F0.wireOp",EDGE,"E14.0.1.2"),sQuery(id+"F0.wireOp",EDGE,"E14.0.1.3"),sQuery(id+"F0.wireOp",EDGE,"E15.MirrorCS"),sQuery(id+"F0.wireOp",EDGE,"E16.MirrorCS"),sQuery(id+"F0.wireOp",EDGE,"E17.MirrorCS"),sQuery(id+"F0.wireOp",EDGE,"E18.MirrorCS"),sQuery(id+"F0.wireOp",EDGE,"E19.MirrorCS"),sQuery(id+"F0.wireOp",EDGE,"E20.MirrorCS"),sQuery(id+"F0.wireOp",EDGE,"E21.MirrorCS"),sQuery(id+"F0.wireOp",EDGE,"E23")])],"isStart":true});
            var sketch = newSketch(context, id + "F44", { "sketchPlane" : qUnion([Q0])});
            skLineSegment(sketch, "E290.bottom", {"start": v(-152.4, 101.6) * mm, "end": v(0, 101.6) * mm});
            skLineSegment(sketch, "E290.top", {"start": v(-152.4, 63.5) * mm, "end": v(0, 63.5) * mm});
            skLineSegment(sketch, "E290.left", {"start": v(-152.4, 101.6) * mm, "end": v(-152.4, 63.5) * mm});
            skLineSegment(sketch, "E290.right", {"start": v(0, 101.6) * mm, "end": v(0, 63.5) * mm});
            skSolve(sketch);
        }
        {
            var Q0;
            Q0=makeQuery(id+"F44.imprint","IMPRINT",FACE,{"disambiguationData":[TD([[makeQuery(id+"F44.imprint","IMPRINT",EDGE,{"derivedFrom":sQuery(id+"F44.wireOp",EDGE,"E290.bottom")}),1.0]])]});
            extrude(context, id + "F45", {"entities" : qUnion([Q0]), "operationType" : NewBodyOperationType.REMOVE, "endBound" : BoundingType.UP_TO_NEXT, "oppositeDirection" : true, "depth" : 25.4 * mm});
        }
        {
            var Q0;
            Q0=makeQuery(id+"F3.opExtrude","CAP_FACE",FACE,{"disambiguationData":[OSD([sQuery(id+"F2.wireOp",EDGE,"E24.bottom"),sQuery(id+"F2.wireOp",EDGE,"E24.top"),sQuery(id+"F2.wireOp",EDGE,"E24.left"),sQuery(id+"F2.wireOp",EDGE,"E24.right"),sQuery(id+"F2.wireOp",EDGE,"E26.bottom"),sQuery(id+"F2.wireOp",EDGE,"E26.top"),sQuery(id+"F2.wireOp",EDGE,"E26.left"),sQuery(id+"F2.wireOp",EDGE,"E26.right"),sQuery(id+"F2.wireOp",EDGE,"E27.bottom"),sQuery(id+"F2.wireOp",EDGE,"E27.top"),sQuery(id+"F2.wireOp",EDGE,"E27.left"),sQuery(id+"F2.wireOp",EDGE,"E27.right"),sQuery(id+"F2.wireOp",EDGE,"E28.bottom"),sQuery(id+"F2.wireOp",EDGE,"E28.top"),sQuery(id+"F2.wireOp",EDGE,"E28.left"),sQuery(id+"F2.wireOp",EDGE,"E28.right"),sQuery(id+"F2.wireOp",EDGE,"E30.MirrorCS"),sQuery(id+"F2.wireOp",EDGE,"E31.MirrorCS"),sQuery(id+"F2.wireOp",EDGE,"E32.MirrorCS"),sQuery(id+"F2.wireOp",EDGE,"E33.MirrorCS"),sQuery(id+"F2.wireOp",EDGE,"E34.MirrorCS"),sQuery(id+"F2.wireOp",EDGE,"E35.MirrorCS"),sQuery(id+"F2.wireOp",EDGE,"E36.MirrorCS"),sQuery(id+"F2.wireOp",EDGE,"E37.MirrorCS")])],"isStart":true});
            var sketch = newSketch(context, id + "F46", { "sketchPlane" : qUnion([Q0])});
            skLineSegment(sketch, "E291", {"start": v(-350.78, 63.5) * mm, "end": v(-376.18, 0) * mm});
            skLineSegment(sketch, "E292", {"start": v(-376.18, 0) * mm, "end": v(-350.78, 0) * mm});
            skLineSegment(sketch, "E293", {"start": v(-198.38, 63.5) * mm, "end": v(-172.98, 0) * mm});
            skLineSegment(sketch, "E294", {"start": v(-172.98, 0) * mm, "end": v(-198.38, 0) * mm});
            skLineSegment(sketch, "E295", {"start": v(-198.38, 0) * mm, "end": v(-198.38, 63.5) * mm});
            skLineSegment(sketch, "E296", {"start": v(-350.78, 63.5) * mm, "end": v(-350.78, 0) * mm});
            skSolve(sketch);
        }
        {
            var Q0;
            Q0=makeQuery(id+"F46.imprint","IMPRINT",FACE,{"disambiguationData":[TD([[makeQuery(id+"F46.imprint","IMPRINT",EDGE,{"derivedFrom":sQuery(id+"F46.wireOp",EDGE,"E291")}),1.0]])]});
            var Q1;
            Q1=makeQuery(id+"F46.imprint","IMPRINT",FACE,{"disambiguationData":[TD([[makeQuery(id+"F46.imprint","IMPRINT",EDGE,{"derivedFrom":sQuery(id+"F46.wireOp",EDGE,"E293")}),-1.0]])]});
            extrude(context, id + "F47", {"entities" : qUnion([Q0, Q1]), "operationType" : NewBodyOperationType.ADD, "oppositeDirection" : true, "depth" : 6.35 * mm});
        }
        {
            var Q0;
            {var subQ0=sQuery(id+"F42.wireOp",EDGE,"E289.top");Q0=makeQuery(id+"F47.boolean.opBoolean","MERGE",EDGE,{"derivedFrom":[makeQuery(id+"F43.boolean.opBoolean","COPY",EDGE,{"derivedFrom":makeQuery(id+"F43.opExtrude","SWEPT_EDGE",EDGE,{"disambiguationData":[OSD([sQuery(id+"F2.wireOp",EDGE,"E24.right"),subQ0,sQuery(id+"F42.wireOp",EDGE,"E289.left")])]})}),makeQuery(id+"F47.opExtrude","SWEPT_EDGE",EDGE,{"disambiguationData":[OSD([subQ0,sQuery(id+"F46.wireOp",EDGE,"E291"),sQuery(id+"F46.wireOp",EDGE,"E296")])]})]});}
            var Q1;
            {var subQ0=sQuery(id+"F42.wireOp",EDGE,"E289.top");Q1=makeQuery(id+"F47.boolean.opBoolean","MERGE",EDGE,{"derivedFrom":[makeQuery(id+"F43.boolean.opBoolean","COPY",EDGE,{"derivedFrom":makeQuery(id+"F43.opExtrude","SWEPT_EDGE",EDGE,{"disambiguationData":[OSD([sQuery(id+"F2.wireOp",EDGE,"E24.left"),subQ0,sQuery(id+"F42.wireOp",EDGE,"E289.right")])]})}),makeQuery(id+"F47.opExtrude","SWEPT_EDGE",EDGE,{"disambiguationData":[OSD([subQ0,sQuery(id+"F46.wireOp",EDGE,"E293"),sQuery(id+"F46.wireOp",EDGE,"E295")])]})]});}
            var Q2;
            Q2=makeQuery(id+"F47.opExtrude","SWEPT_EDGE",EDGE,{"disambiguationData":[OSD([sQuery(id+"F46.wireOp",EDGE,"E291"),sQuery(id+"F46.wireOp",EDGE,"E292")])]});
            var Q3;
            Q3=makeQuery(id+"F47.opExtrude","SWEPT_EDGE",EDGE,{"disambiguationData":[OSD([sQuery(id+"F46.wireOp",EDGE,"E293"),sQuery(id+"F46.wireOp",EDGE,"E294")])]});
            fillet(context, id + "F48", {"entities" : qUnion([Q0, Q1, Q2, Q3]), "radius" : 5.08 * mm, "tangentPropagation" : true, "allowEdgeOverflow" : false});
        }
        {
            var Q0;
            Q0=makeQuery(id+"F1.opExtrude","CAP_FACE",FACE,{"disambiguationData":[OSD([sQuery(id+"F0.wireOp",EDGE,"E0.bottom"),sQuery(id+"F0.wireOp",EDGE,"E0.top"),sQuery(id+"F0.wireOp",EDGE,"E0.left"),sQuery(id+"F0.wireOp",EDGE,"E0.right"),sQuery(id+"F0.wireOp",EDGE,"E11.1.0.0"),sQuery(id+"F0.wireOp",EDGE,"E11.1.0.1"),sQuery(id+"F0.wireOp",EDGE,"E11.1.0.2"),sQuery(id+"F0.wireOp",EDGE,"E11.1.0.3"),sQuery(id+"F0.wireOp",EDGE,"E11.1.0.4"),sQuery(id+"F0.wireOp",EDGE,"E11.1.0.5"),sQuery(id+"F0.wireOp",EDGE,"E11.1.0.6"),sQuery(id+"F0.wireOp",EDGE,"E11.1.0.7"),sQuery(id+"F0.wireOp",EDGE,"E11.2.0.0"),sQuery(id+"F0.wireOp",EDGE,"E11.2.0.1"),sQuery(id+"F0.wireOp",EDGE,"E11.2.0.2"),sQuery(id+"F0.wireOp",EDGE,"E11.2.0.3"),sQuery(id+"F0.wireOp",EDGE,"E11.2.0.4"),sQuery(id+"F0.wireOp",EDGE,"E11.2.0.5"),sQuery(id+"F0.wireOp",EDGE,"E11.2.0.6"),sQuery(id+"F0.wireOp",EDGE,"E11.2.0.7"),sQuery(id+"F0.wireOp",EDGE,"E12.0.0.1"),sQuery(id+"F0.wireOp",EDGE,"E12.3.0.1"),sQuery(id+"F0.wireOp",EDGE,"E12.6.0.1"),sQuery(id+"F0.wireOp",EDGE,"E12.9.0.1"),sQuery(id+"F0.wireOp",EDGE,"E12.12.0.1"),sQuery(id+"F0.wireOp",EDGE,"E12.15.0.1"),sQuery(id+"F0.wireOp",EDGE,"E12.18.0.1"),sQuery(id+"F0.wireOp",EDGE,"E12.21.0.1"),sQuery(id+"F0.wireOp",EDGE,"E12.0.1.1"),sQuery(id+"F0.wireOp",EDGE,"E12.3.1.1"),sQuery(id+"F0.wireOp",EDGE,"E12.6.1.1"),sQuery(id+"F0.wireOp",EDGE,"E12.9.1.1"),sQuery(id+"F0.wireOp",EDGE,"E12.12.1.1"),sQuery(id+"F0.wireOp",EDGE,"E12.15.1.1"),sQuery(id+"F0.wireOp",EDGE,"E12.18.1.1"),sQuery(id+"F0.wireOp",EDGE,"E12.21.1.1"),sQuery(id+"F0.wireOp",EDGE,"E3"),sQuery(id+"F0.wireOp",EDGE,"E6.MirrorCS"),sQuery(id+"F0.wireOp",EDGE,"E5.MirrorCS"),sQuery(id+"F0.wireOp",EDGE,"E10.MirrorCS"),sQuery(id+"F0.wireOp",EDGE,"E9.MirrorCS"),sQuery(id+"F0.wireOp",EDGE,"E8.MirrorCS"),sQuery(id+"F0.wireOp",EDGE,"E7.MirrorCS"),sQuery(id+"F0.wireOp",EDGE,"E4"),sQuery(id+"F0.wireOp",EDGE,"E13.bottom"),sQuery(id+"F0.wireOp",EDGE,"E13.top"),sQuery(id+"F0.wireOp",EDGE,"E13.left"),sQuery(id+"F0.wireOp",EDGE,"E13.right"),sQuery(id+"F0.wireOp",EDGE,"E14.0.1.0"),sQuery(id+"F0.wireOp",EDGE,"E14.0.1.1"),sQuery(id+"F0.wireOp",EDGE,"E14.0.1.2"),sQuery(id+"F0.wireOp",EDGE,"E14.0.1.3"),sQuery(id+"F0.wireOp",EDGE,"E15.MirrorCS"),sQuery(id+"F0.wireOp",EDGE,"E16.MirrorCS"),sQuery(id+"F0.wireOp",EDGE,"E17.MirrorCS"),sQuery(id+"F0.wireOp",EDGE,"E18.MirrorCS"),sQuery(id+"F0.wireOp",EDGE,"E19.MirrorCS"),sQuery(id+"F0.wireOp",EDGE,"E20.MirrorCS"),sQuery(id+"F0.wireOp",EDGE,"E21.MirrorCS"),sQuery(id+"F0.wireOp",EDGE,"E23")])],"isStart":true});
            var sketch = newSketch(context, id + "F49", { "sketchPlane" : qUnion([Q0])});
            skLineSegment(sketch, "E297", {"start": v(-152.4, 63.5) * mm, "end": v(-177.8, 0) * mm});
            skLineSegment(sketch, "E298", {"start": v(-177.8, 0) * mm, "end": v(-152.4, 0) * mm});
            skLineSegment(sketch, "E299", {"start": v(-152.4, 0) * mm, "end": v(-152.4, 63.5) * mm});
            skLineSegment(sketch, "E300", {"start": v(0, 63.5) * mm, "end": v(0, 0) * mm});
            skLineSegment(sketch, "E301", {"start": v(0, 0) * mm, "end": v(25.4, 0) * mm});
            skLineSegment(sketch, "E302", {"start": v(25.4, 0) * mm, "end": v(0, 63.5) * mm});
            skSolve(sketch);
        }
        {
            var Q0;
            Q0=makeQuery(id+"F49.imprint","IMPRINT",FACE,{"disambiguationData":[TD([[makeQuery(id+"F49.imprint","IMPRINT",EDGE,{"derivedFrom":sQuery(id+"F49.wireOp",EDGE,"E297")}),1.0]])]});
            var Q1;
            Q1=makeQuery(id+"F49.imprint","IMPRINT",FACE,{"disambiguationData":[TD([[makeQuery(id+"F49.imprint","IMPRINT",EDGE,{"derivedFrom":sQuery(id+"F49.wireOp",EDGE,"E300")}),-1.0]])]});
            extrude(context, id + "F50", {"entities" : qUnion([Q0, Q1]), "operationType" : NewBodyOperationType.ADD, "oppositeDirection" : true, "depth" : 6.35 * mm});
        }
        {
            var Q0;
            {var subQ0=sQuery(id+"F44.wireOp",EDGE,"E290.top");Q0=makeQuery(id+"F50.boolean.opBoolean","MERGE",EDGE,{"derivedFrom":[makeQuery(id+"F45.boolean.opBoolean","COPY",EDGE,{"derivedFrom":makeQuery(id+"F45.opExtrude","SWEPT_EDGE",EDGE,{"disambiguationData":[OSD([sQuery(id+"F0.wireOp",EDGE,"E0.right"),subQ0,sQuery(id+"F44.wireOp",EDGE,"E290.left")])]})}),makeQuery(id+"F50.opExtrude","SWEPT_EDGE",EDGE,{"disambiguationData":[OSD([subQ0,sQuery(id+"F49.wireOp",EDGE,"E297"),sQuery(id+"F49.wireOp",EDGE,"E299")])]})]});}
            var Q1;
            {var subQ0=sQuery(id+"F44.wireOp",EDGE,"E290.top");Q1=makeQuery(id+"F50.boolean.opBoolean","MERGE",EDGE,{"derivedFrom":[makeQuery(id+"F45.boolean.opBoolean","COPY",EDGE,{"derivedFrom":makeQuery(id+"F45.opExtrude","SWEPT_EDGE",EDGE,{"disambiguationData":[OSD([sQuery(id+"F0.wireOp",EDGE,"E0.left"),subQ0,sQuery(id+"F44.wireOp",EDGE,"E290.right")])]})}),makeQuery(id+"F50.opExtrude","SWEPT_EDGE",EDGE,{"disambiguationData":[OSD([subQ0,sQuery(id+"F49.wireOp",EDGE,"E300"),sQuery(id+"F49.wireOp",EDGE,"E302")])]})]});}
            var Q2;
            Q2=makeQuery(id+"F50.opExtrude","SWEPT_EDGE",EDGE,{"disambiguationData":[OSD([sQuery(id+"F49.wireOp",EDGE,"E301"),sQuery(id+"F49.wireOp",EDGE,"E302")])]});
            var Q3;
            Q3=makeQuery(id+"F50.opExtrude","SWEPT_EDGE",EDGE,{"disambiguationData":[OSD([sQuery(id+"F49.wireOp",EDGE,"E297"),sQuery(id+"F49.wireOp",EDGE,"E298")])]});
            fillet(context, id + "F51", {"entities" : qUnion([Q0, Q1, Q2, Q3]), "radius" : 5.08 * mm, "tangentPropagation" : true, "allowEdgeOverflow" : false});
        }
        {
            var Q0;
            Q0=qCreatedBy(makeId("Right.planeOp"),FACE);
            var sketch = newSketch(context, id + "F52", { "sketchPlane" : qUnion([Q0])});
            skCircle(sketch, "E303", {"center": v(-40.92, 0) * mm, "radius": 12.7 * mm});
            skCircle(sketch, "E304", {"center": v(-40.92, 7.3) * mm, "radius": 1.52 * mm});
            skLineSegment(sketch, "E305", {"start": v(-40.92, 0) * mm, "end": v(-40.92, 7.3) * mm, "construction": true});
            skLineSegment(sketch, "E306", {"start": v(-40.92, 7.3) * mm, "end": v(-40.92, 0) * mm, "construction": true});
            skCircle(sketch, "E307.MirrorC", {"center": v(-40.92, -7.3) * mm, "radius": 1.52 * mm});
            skCircle(sketch, "E308", {"center": v(-40.92, 0) * mm, "radius": 4.45 * mm});
            skSolve(sketch);
        }
        {
            var Q0;
            Q0=makeQuery(id+"F52.imprint","IMPRINT",FACE,{"disambiguationData":[TD([[makeQuery(id+"F52.imprint","IMPRINT",EDGE,{"derivedFrom":sQuery(id+"F52.wireOp",EDGE,"E303")}),1.0]])]});
            extrude(context, id + "F53", {"entities" : qUnion([Q0]), "depth" : 6.35 * mm});
        }
    });
